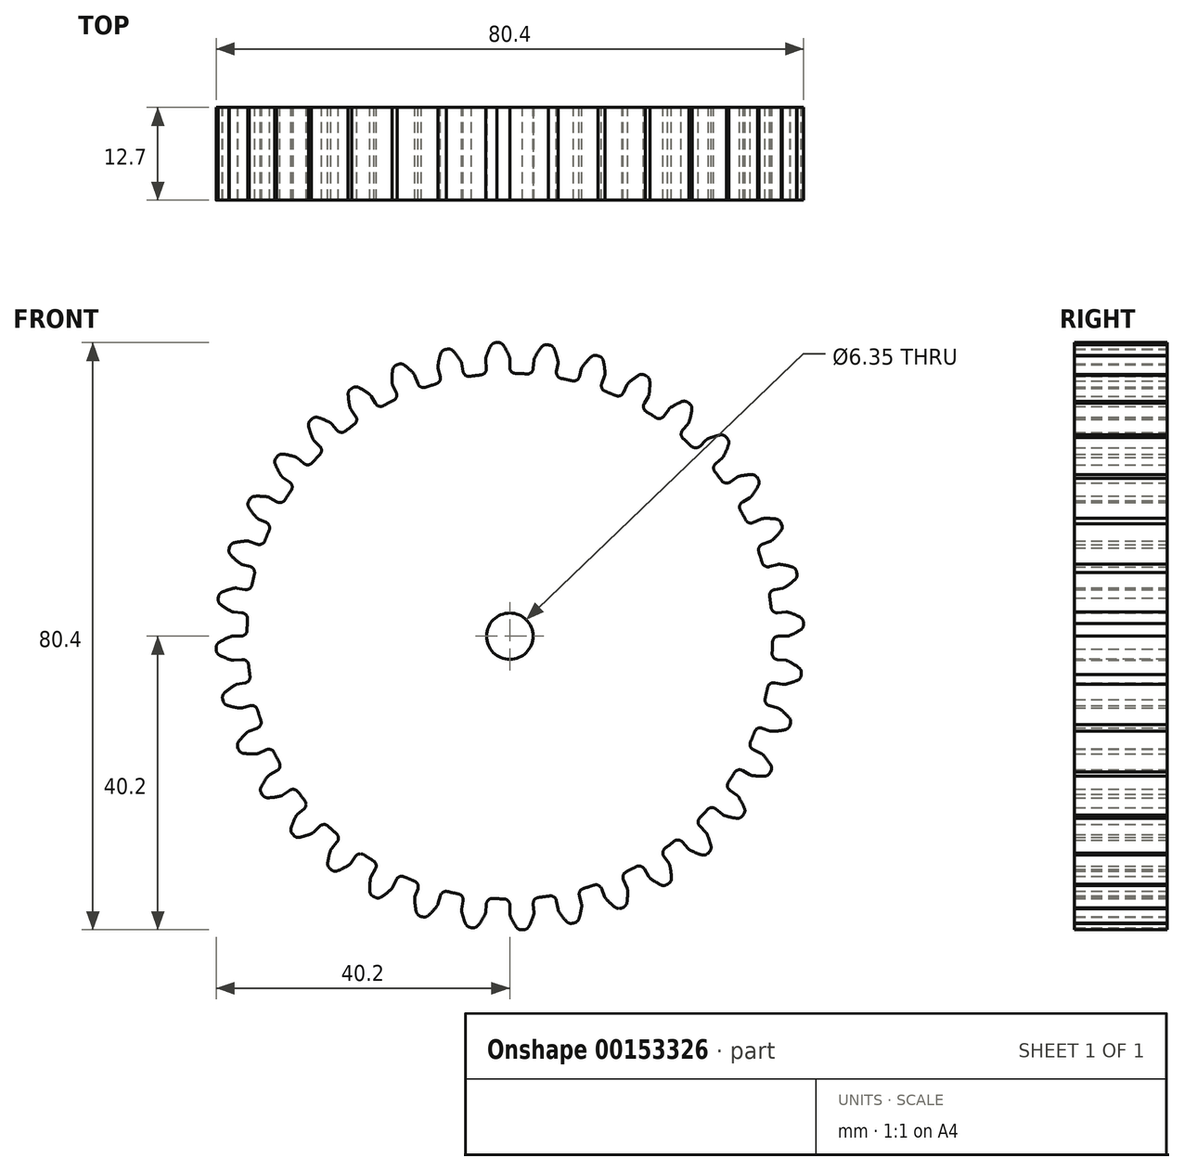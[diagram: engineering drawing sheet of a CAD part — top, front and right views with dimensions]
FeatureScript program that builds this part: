
annotation { "Feature Type Name" : "Feature", "Feature Type Description" : "" }
export const myFeature = defineFeature(function(context is Context, id is Id, definition is map)
    precondition{}
    {
        {
            var Q0;
            Q0=qCreatedBy(makeId("Front.planeOp"),FACE);
            var sketch = newSketch(context, id + "F0", { "sketchPlane" : qUnion([Q0])});
            skArc(sketch, "E0", {"start": v(-3.94, 35.77) * mm, "mid": v(-4.7, 35.68) * mm, "end": v(-5.45, 35.57) * mm});
            skLineSegment(sketch, "E1", {"start": v(-1.57, 40.2) * mm, "end": v(-1.76, 40.2) * mm});
            skLineSegment(sketch, "E2", {"start": v(0, 37.94) * mm, "end": v(0, 36.8) * mm});
            skArc(sketch, "E3.trimOffspring", {"start": v(-0.06, 38.25) * mm, "mid": v(-0.43, 39.06) * mm, "end": v(-0.87, 39.82) * mm});
            skLineSegment(sketch, "E4.MirrorCS", {"start": v(-1.94, 40.18) * mm, "end": v(-1.76, 40.2) * mm});
            skArc(sketch, "E5.MirrorCS", {"start": v(-3.27, 38.11) * mm, "mid": v(-2.98, 38.94) * mm, "end": v(-2.6, 39.75) * mm});
            skLineSegment(sketch, "E6.MirrorCS", {"start": v(-3.3, 37.8) * mm, "end": v(-3.2, 36.66) * mm});
            skPoint(sketch, "E7.visualSharp", {"position": v(0, 35.98) * mm});
            skArc(sketch, "E7.filletArc", {"start": v(0, 36.8) * mm, "mid": v(0.24, 36.22) * mm, "end": v(0.8, 35.97) * mm});
            skPoint(sketch, "E8.visualSharp", {"position": v(-3.14, 35.85) * mm});
            skArc(sketch, "E8.filletArc", {"start": v(-3.94, 35.77) * mm, "mid": v(-3.4, 36.06) * mm, "end": v(-3.2, 36.66) * mm});
            skPoint(sketch, "E9.visualSharp", {"position": v(-3.32, 37.96) * mm});
            skArc(sketch, "E9.filletArc", {"start": v(-3.27, 38.11) * mm, "mid": v(-3.3, 37.96) * mm, "end": v(-3.3, 37.8) * mm});
            skPoint(sketch, "E10.visualSharp", {"position": v(0, 38.1) * mm});
            skArc(sketch, "E10.filletArc", {"start": v(0, 37.94) * mm, "mid": v(-0.02, 38.1) * mm, "end": v(-0.06, 38.25) * mm});
            skPoint(sketch, "E11.visualSharp", {"position": v(-2.38, 40.15) * mm});
            skArc(sketch, "E11.filletArc", {"start": v(-1.94, 40.18) * mm, "mid": v(-2.33, 40.05) * mm, "end": v(-2.6, 39.75) * mm});
            skPoint(sketch, "E12.visualSharp", {"position": v(-1.13, 40.2) * mm});
            skArc(sketch, "E12.filletArc", {"start": v(-0.87, 39.82) * mm, "mid": v(-1.17, 40.1) * mm, "end": v(-1.57, 40.2) * mm});
            skArc(sketch, "E13.1.0", {"start": v(-10.1, 34.54) * mm, "mid": v(-9.6, 34.93) * mm, "end": v(-9.52, 35.55) * mm});
            skLineSegment(sketch, "E13.1.1", {"start": v(-9.82, 36.65) * mm, "end": v(-9.52, 35.55) * mm});
            skArc(sketch, "E13.1.2", {"start": v(-9.84, 36.96) * mm, "mid": v(-9.85, 36.8) * mm, "end": v(-9.82, 36.65) * mm});
            skArc(sketch, "E13.1.3", {"start": v(-9.84, 36.96) * mm, "mid": v(-9.7, 37.84) * mm, "end": v(-9.47, 38.69) * mm});
            skArc(sketch, "E13.1.4", {"start": v(-8.9, 39.24) * mm, "mid": v(-9.25, 39.04) * mm, "end": v(-9.47, 38.69) * mm});
            skLineSegment(sketch, "E13.1.5", {"start": v(-8.9, 39.24) * mm, "end": v(-8.7, 39.29) * mm});
            skLineSegment(sketch, "E13.1.6", {"start": v(-8.52, 39.32) * mm, "end": v(-8.7, 39.29) * mm});
            skArc(sketch, "E13.1.7", {"start": v(-7.77, 39.06) * mm, "mid": v(-8.12, 39.29) * mm, "end": v(-8.52, 39.32) * mm});
            skArc(sketch, "E13.1.8", {"start": v(-6.7, 37.66) * mm, "mid": v(-7.2, 38.39) * mm, "end": v(-7.77, 39.06) * mm});
            skArc(sketch, "E13.1.9", {"start": v(-6.59, 37.37) * mm, "mid": v(-6.63, 37.52) * mm, "end": v(-6.7, 37.66) * mm});
            skLineSegment(sketch, "E13.1.10", {"start": v(-6.59, 37.37) * mm, "end": v(-6.4, 36.24) * mm});
            skArc(sketch, "E13.1.11", {"start": v(-6.4, 36.24) * mm, "mid": v(-6.06, 35.71) * mm, "end": v(-5.45, 35.57) * mm});
            skArc(sketch, "E13.2.0", {"start": v(-15.93, 32.26) * mm, "mid": v(-15.52, 32.73) * mm, "end": v(-15.55, 33.35) * mm});
            skLineSegment(sketch, "E13.2.1", {"start": v(-16.04, 34.39) * mm, "end": v(-15.55, 33.35) * mm});
            skArc(sketch, "E13.2.2", {"start": v(-16.11, 34.7) * mm, "mid": v(-16.09, 34.54) * mm, "end": v(-16.04, 34.39) * mm});
            skArc(sketch, "E13.2.3", {"start": v(-16.11, 34.7) * mm, "mid": v(-16.12, 35.58) * mm, "end": v(-16.04, 36.46) * mm});
            skArc(sketch, "E13.2.4", {"start": v(-15.57, 37.1) * mm, "mid": v(-15.89, 36.84) * mm, "end": v(-16.04, 36.46) * mm});
            skLineSegment(sketch, "E13.2.5", {"start": v(-15.57, 37.1) * mm, "end": v(-15.4, 37.18) * mm});
            skLineSegment(sketch, "E13.2.6", {"start": v(-15.22, 37.24) * mm, "end": v(-15.4, 37.18) * mm});
            skArc(sketch, "E13.2.7", {"start": v(-14.44, 37.12) * mm, "mid": v(-14.81, 37.28) * mm, "end": v(-15.22, 37.24) * mm});
            skArc(sketch, "E13.2.8", {"start": v(-13.14, 35.93) * mm, "mid": v(-13.76, 36.55) * mm, "end": v(-14.44, 37.12) * mm});
            skArc(sketch, "E13.2.9", {"start": v(-12.98, 35.65) * mm, "mid": v(-13.05, 35.8) * mm, "end": v(-13.14, 35.93) * mm});
            skLineSegment(sketch, "E13.2.10", {"start": v(-12.98, 35.65) * mm, "end": v(-12.59, 34.58) * mm});
            skArc(sketch, "E13.2.11", {"start": v(-12.59, 34.58) * mm, "mid": v(-12.17, 34.12) * mm, "end": v(-11.55, 34.08) * mm});
            skArc(sketch, "E13.3.0", {"start": v(-21.3, 29) * mm, "mid": v(-20.97, 29.54) * mm, "end": v(-21.1, 30.14) * mm});
            skLineSegment(sketch, "E13.3.1", {"start": v(-21.76, 31.08) * mm, "end": v(-21.1, 30.14) * mm});
            skArc(sketch, "E13.3.2", {"start": v(-21.9, 31.37) * mm, "mid": v(-21.84, 31.22) * mm, "end": v(-21.76, 31.08) * mm});
            skArc(sketch, "E13.3.3", {"start": v(-21.9, 31.37) * mm, "mid": v(-22.05, 32.24) * mm, "end": v(-22.13, 33.12) * mm});
            skArc(sketch, "E13.3.4", {"start": v(-21.78, 33.83) * mm, "mid": v(-22.04, 33.52) * mm, "end": v(-22.13, 33.12) * mm});
            skLineSegment(sketch, "E13.3.5", {"start": v(-21.78, 33.83) * mm, "end": v(-21.62, 33.94) * mm});
            skLineSegment(sketch, "E13.3.6", {"start": v(-21.46, 34.03) * mm, "end": v(-21.62, 33.94) * mm});
            skArc(sketch, "E13.3.7", {"start": v(-20.66, 34.05) * mm, "mid": v(-21.06, 34.14) * mm, "end": v(-21.46, 34.03) * mm});
            skArc(sketch, "E13.3.8", {"start": v(-19.18, 33.1) * mm, "mid": v(-19.9, 33.6) * mm, "end": v(-20.66, 34.05) * mm});
            skArc(sketch, "E13.3.9", {"start": v(-18.97, 32.86) * mm, "mid": v(-19.06, 32.99) * mm, "end": v(-19.18, 33.1) * mm});
            skLineSegment(sketch, "E13.3.10", {"start": v(-18.97, 32.86) * mm, "end": v(-18.4, 31.87) * mm});
            skArc(sketch, "E13.3.11", {"start": v(-18.4, 31.87) * mm, "mid": v(-17.9, 31.49) * mm, "end": v(-17.29, 31.56) * mm});
            skArc(sketch, "E13.4.0", {"start": v(-26, 24.87) * mm, "mid": v(-25.78, 25.45) * mm, "end": v(-26.02, 26.02) * mm});
            skLineSegment(sketch, "E13.4.1", {"start": v(-26.83, 26.83) * mm, "end": v(-26.02, 26.02) * mm});
            skArc(sketch, "E13.4.2", {"start": v(-27, 27.1) * mm, "mid": v(-26.93, 26.95) * mm, "end": v(-26.83, 26.83) * mm});
            skArc(sketch, "E13.4.3", {"start": v(-27, 27.1) * mm, "mid": v(-27.31, 27.92) * mm, "end": v(-27.54, 28.77) * mm});
            skArc(sketch, "E13.4.4", {"start": v(-27.32, 29.53) * mm, "mid": v(-27.53, 29.18) * mm, "end": v(-27.54, 28.77) * mm});
            skLineSegment(sketch, "E13.4.5", {"start": v(-27.32, 29.53) * mm, "end": v(-27.19, 29.67) * mm});
            skLineSegment(sketch, "E13.4.6", {"start": v(-27.04, 29.79) * mm, "end": v(-27.19, 29.67) * mm});
            skArc(sketch, "E13.4.7", {"start": v(-26.26, 29.94) * mm, "mid": v(-26.67, 29.97) * mm, "end": v(-27.04, 29.79) * mm});
            skArc(sketch, "E13.4.8", {"start": v(-24.63, 29.26) * mm, "mid": v(-25.43, 29.64) * mm, "end": v(-26.26, 29.94) * mm});
            skArc(sketch, "E13.4.9", {"start": v(-24.39, 29.07) * mm, "mid": v(-24.5, 29.18) * mm, "end": v(-24.63, 29.26) * mm});
            skLineSegment(sketch, "E13.4.10", {"start": v(-24.39, 29.07) * mm, "end": v(-23.65, 28.2) * mm});
            skArc(sketch, "E13.4.11", {"start": v(-23.65, 28.2) * mm, "mid": v(-23.1, 27.9) * mm, "end": v(-22.5, 28.08) * mm});
            skArc(sketch, "E13.5.0", {"start": v(-29.93, 19.97) * mm, "mid": v(-29.8, 20.58) * mm, "end": v(-30.14, 21.1) * mm});
            skLineSegment(sketch, "E13.5.1", {"start": v(-31.08, 21.76) * mm, "end": v(-30.14, 21.1) * mm});
            skArc(sketch, "E13.5.2", {"start": v(-31.3, 22) * mm, "mid": v(-31.2, 21.87) * mm, "end": v(-31.08, 21.76) * mm});
            skArc(sketch, "E13.5.3", {"start": v(-31.3, 22) * mm, "mid": v(-31.75, 22.75) * mm, "end": v(-32.12, 23.55) * mm});
            skArc(sketch, "E13.5.4", {"start": v(-32.03, 24.34) * mm, "mid": v(-32.18, 23.96) * mm, "end": v(-32.12, 23.55) * mm});
            skLineSegment(sketch, "E13.5.5", {"start": v(-32.03, 24.34) * mm, "end": v(-31.92, 24.5) * mm});
            skLineSegment(sketch, "E13.5.6", {"start": v(-31.8, 24.64) * mm, "end": v(-31.92, 24.5) * mm});
            skArc(sketch, "E13.5.7", {"start": v(-31.06, 24.93) * mm, "mid": v(-31.47, 24.88) * mm, "end": v(-31.8, 24.64) * mm});
            skArc(sketch, "E13.5.8", {"start": v(-29.34, 24.54) * mm, "mid": v(-30.2, 24.78) * mm, "end": v(-31.06, 24.93) * mm});
            skArc(sketch, "E13.5.9", {"start": v(-29.07, 24.39) * mm, "mid": v(-29.2, 24.48) * mm, "end": v(-29.34, 24.54) * mm});
            skLineSegment(sketch, "E13.5.10", {"start": v(-29.07, 24.39) * mm, "end": v(-28.2, 23.65) * mm});
            skArc(sketch, "E13.5.11", {"start": v(-28.2, 23.65) * mm, "mid": v(-27.6, 23.46) * mm, "end": v(-27.04, 23.74) * mm});
            skArc(sketch, "E13.6.0", {"start": v(-32.94, 14.47) * mm, "mid": v(-32.93, 15.1) * mm, "end": v(-33.35, 15.55) * mm});
            skLineSegment(sketch, "E13.6.1", {"start": v(-34.39, 16.04) * mm, "end": v(-33.35, 15.55) * mm});
            skArc(sketch, "E13.6.2", {"start": v(-34.64, 16.22) * mm, "mid": v(-34.52, 16.12) * mm, "end": v(-34.39, 16.04) * mm});
            skArc(sketch, "E13.6.3", {"start": v(-34.64, 16.22) * mm, "mid": v(-35.21, 16.9) * mm, "end": v(-35.72, 17.62) * mm});
            skArc(sketch, "E13.6.4", {"start": v(-35.77, 18.4) * mm, "mid": v(-35.85, 18) * mm, "end": v(-35.72, 17.62) * mm});
            skLineSegment(sketch, "E13.6.5", {"start": v(-35.77, 18.4) * mm, "end": v(-35.7, 18.58) * mm});
            skLineSegment(sketch, "E13.6.6", {"start": v(-35.6, 18.74) * mm, "end": v(-35.7, 18.58) * mm});
            skArc(sketch, "E13.6.7", {"start": v(-34.92, 19.16) * mm, "mid": v(-35.31, 19.04) * mm, "end": v(-35.6, 18.74) * mm});
            skArc(sketch, "E13.6.8", {"start": v(-33.16, 19.07) * mm, "mid": v(-34.04, 19.16) * mm, "end": v(-34.92, 19.16) * mm});
            skArc(sketch, "E13.6.9", {"start": v(-32.86, 18.97) * mm, "mid": v(-33, 19.04) * mm, "end": v(-33.16, 19.07) * mm});
            skLineSegment(sketch, "E13.6.10", {"start": v(-32.86, 18.97) * mm, "end": v(-31.87, 18.4) * mm});
            skArc(sketch, "E13.6.11", {"start": v(-31.87, 18.4) * mm, "mid": v(-31.25, 18.31) * mm, "end": v(-30.75, 18.69) * mm});
            skArc(sketch, "E13.7.0", {"start": v(-34.96, 8.53) * mm, "mid": v(-35.05, 9.15) * mm, "end": v(-35.55, 9.52) * mm});
            skLineSegment(sketch, "E13.7.1", {"start": v(-36.65, 9.82) * mm, "end": v(-35.55, 9.52) * mm});
            skArc(sketch, "E13.7.2", {"start": v(-36.93, 9.96) * mm, "mid": v(-36.8, 9.88) * mm, "end": v(-36.65, 9.82) * mm});
            skArc(sketch, "E13.7.3", {"start": v(-36.93, 9.96) * mm, "mid": v(-37.61, 10.52) * mm, "end": v(-38.24, 11.15) * mm});
            skArc(sketch, "E13.7.4", {"start": v(-38.43, 11.92) * mm, "mid": v(-38.43, 11.5) * mm, "end": v(-38.24, 11.15) * mm});
            skLineSegment(sketch, "E13.7.5", {"start": v(-38.43, 11.92) * mm, "end": v(-38.38, 12.1) * mm});
            skLineSegment(sketch, "E13.7.6", {"start": v(-38.31, 12.28) * mm, "end": v(-38.38, 12.1) * mm});
            skArc(sketch, "E13.7.7", {"start": v(-37.72, 12.8) * mm, "mid": v(-38.08, 12.62) * mm, "end": v(-38.31, 12.28) * mm});
            skArc(sketch, "E13.7.8", {"start": v(-35.97, 13.03) * mm, "mid": v(-36.85, 12.95) * mm, "end": v(-37.72, 12.8) * mm});
            skArc(sketch, "E13.7.9", {"start": v(-35.65, 12.98) * mm, "mid": v(-35.8, 13.02) * mm, "end": v(-35.97, 13.03) * mm});
            skLineSegment(sketch, "E13.7.10", {"start": v(-35.65, 12.98) * mm, "end": v(-34.58, 12.59) * mm});
            skArc(sketch, "E13.7.11", {"start": v(-34.58, 12.59) * mm, "mid": v(-33.96, 12.6) * mm, "end": v(-33.53, 13.06) * mm});
            skArc(sketch, "E13.8.0", {"start": v(-35.9, 2.33) * mm, "mid": v(-36.1, 2.92) * mm, "end": v(-36.66, 3.2) * mm});
            skLineSegment(sketch, "E13.8.1", {"start": v(-37.8, 3.3) * mm, "end": v(-36.66, 3.2) * mm});
            skArc(sketch, "E13.8.2", {"start": v(-38.1, 3.4) * mm, "mid": v(-37.95, 3.34) * mm, "end": v(-37.8, 3.3) * mm});
            skArc(sketch, "E13.8.3", {"start": v(-38.1, 3.4) * mm, "mid": v(-38.87, 3.83) * mm, "end": v(-39.6, 4.34) * mm});
            skArc(sketch, "E13.8.4", {"start": v(-39.91, 5.06) * mm, "mid": v(-39.85, 4.66) * mm, "end": v(-39.6, 4.34) * mm});
            skLineSegment(sketch, "E13.8.5", {"start": v(-39.91, 5.06) * mm, "end": v(-39.9, 5.25) * mm});
            skLineSegment(sketch, "E13.8.6", {"start": v(-39.86, 5.44) * mm, "end": v(-39.9, 5.25) * mm});
            skArc(sketch, "E13.8.7", {"start": v(-39.37, 6.06) * mm, "mid": v(-39.7, 5.81) * mm, "end": v(-39.86, 5.44) * mm});
            skArc(sketch, "E13.8.8", {"start": v(-37.68, 6.58) * mm, "mid": v(-38.54, 6.36) * mm, "end": v(-39.37, 6.06) * mm});
            skArc(sketch, "E13.8.9", {"start": v(-37.37, 6.59) * mm, "mid": v(-37.52, 6.6) * mm, "end": v(-37.68, 6.58) * mm});
            skLineSegment(sketch, "E13.8.10", {"start": v(-37.37, 6.59) * mm, "end": v(-36.24, 6.4) * mm});
            skArc(sketch, "E13.8.11", {"start": v(-36.24, 6.4) * mm, "mid": v(-35.63, 6.52) * mm, "end": v(-35.29, 7.04) * mm});
            skArc(sketch, "E13.9.0", {"start": v(-35.77, -3.94) * mm, "mid": v(-36.06, -3.4) * mm, "end": v(-36.66, -3.2) * mm});
            skLineSegment(sketch, "E13.9.1", {"start": v(-37.8, -3.3) * mm, "end": v(-36.66, -3.2) * mm});
            skArc(sketch, "E13.9.2", {"start": v(-38.11, -3.27) * mm, "mid": v(-37.96, -3.3) * mm, "end": v(-37.8, -3.3) * mm});
            skArc(sketch, "E13.9.3", {"start": v(-38.11, -3.27) * mm, "mid": v(-38.94, -2.98) * mm, "end": v(-39.75, -2.6) * mm});
            skArc(sketch, "E13.9.4", {"start": v(-40.18, -1.94) * mm, "mid": v(-40.05, -2.33) * mm, "end": v(-39.75, -2.6) * mm});
            skLineSegment(sketch, "E13.9.5", {"start": v(-40.18, -1.94) * mm, "end": v(-40.2, -1.76) * mm});
            skLineSegment(sketch, "E13.9.6", {"start": v(-40.2, -1.57) * mm, "end": v(-40.2, -1.76) * mm});
            skArc(sketch, "E13.9.7", {"start": v(-39.82, -0.87) * mm, "mid": v(-40.1, -1.17) * mm, "end": v(-40.2, -1.57) * mm});
            skArc(sketch, "E13.9.8", {"start": v(-38.25, -0.06) * mm, "mid": v(-39.06, -0.43) * mm, "end": v(-39.82, -0.87) * mm});
            skArc(sketch, "E13.9.9", {"start": v(-37.94, 0) * mm, "mid": v(-38.1, -0.02) * mm, "end": v(-38.25, -0.06) * mm});
            skLineSegment(sketch, "E13.9.10", {"start": v(-37.94, 0) * mm, "end": v(-36.8, 0) * mm});
            skArc(sketch, "E13.9.11", {"start": v(-36.8, 0) * mm, "mid": v(-36.22, 0.24) * mm, "end": v(-35.97, 0.8) * mm});
            skArc(sketch, "E13.10.0", {"start": v(-34.54, -10.1) * mm, "mid": v(-34.93, -9.6) * mm, "end": v(-35.55, -9.52) * mm});
            skLineSegment(sketch, "E13.10.1", {"start": v(-36.65, -9.82) * mm, "end": v(-35.55, -9.52) * mm});
            skArc(sketch, "E13.10.2", {"start": v(-36.96, -9.84) * mm, "mid": v(-36.8, -9.85) * mm, "end": v(-36.65, -9.82) * mm});
            skArc(sketch, "E13.10.3", {"start": v(-36.96, -9.84) * mm, "mid": v(-37.84, -9.7) * mm, "end": v(-38.69, -9.47) * mm});
            skArc(sketch, "E13.10.4", {"start": v(-39.24, -8.9) * mm, "mid": v(-39.04, -9.25) * mm, "end": v(-38.69, -9.47) * mm});
            skLineSegment(sketch, "E13.10.5", {"start": v(-39.24, -8.9) * mm, "end": v(-39.29, -8.7) * mm});
            skLineSegment(sketch, "E13.10.6", {"start": v(-39.32, -8.52) * mm, "end": v(-39.29, -8.7) * mm});
            skArc(sketch, "E13.10.7", {"start": v(-39.06, -7.77) * mm, "mid": v(-39.29, -8.12) * mm, "end": v(-39.32, -8.52) * mm});
            skArc(sketch, "E13.10.8", {"start": v(-37.66, -6.7) * mm, "mid": v(-38.39, -7.2) * mm, "end": v(-39.06, -7.77) * mm});
            skArc(sketch, "E13.10.9", {"start": v(-37.37, -6.59) * mm, "mid": v(-37.52, -6.63) * mm, "end": v(-37.66, -6.7) * mm});
            skLineSegment(sketch, "E13.10.10", {"start": v(-37.37, -6.59) * mm, "end": v(-36.24, -6.4) * mm});
            skArc(sketch, "E13.10.11", {"start": v(-36.24, -6.4) * mm, "mid": v(-35.71, -6.06) * mm, "end": v(-35.57, -5.45) * mm});
            skArc(sketch, "E13.11.0", {"start": v(-32.26, -15.93) * mm, "mid": v(-32.73, -15.52) * mm, "end": v(-33.35, -15.55) * mm});
            skLineSegment(sketch, "E13.11.1", {"start": v(-34.39, -16.04) * mm, "end": v(-33.35, -15.55) * mm});
            skArc(sketch, "E13.11.2", {"start": v(-34.7, -16.11) * mm, "mid": v(-34.54, -16.09) * mm, "end": v(-34.39, -16.04) * mm});
            skArc(sketch, "E13.11.3", {"start": v(-34.7, -16.11) * mm, "mid": v(-35.58, -16.12) * mm, "end": v(-36.46, -16.04) * mm});
            skArc(sketch, "E13.11.4", {"start": v(-37.1, -15.57) * mm, "mid": v(-36.84, -15.89) * mm, "end": v(-36.46, -16.04) * mm});
            skLineSegment(sketch, "E13.11.5", {"start": v(-37.1, -15.57) * mm, "end": v(-37.18, -15.4) * mm});
            skLineSegment(sketch, "E13.11.6", {"start": v(-37.24, -15.22) * mm, "end": v(-37.18, -15.4) * mm});
            skArc(sketch, "E13.11.7", {"start": v(-37.12, -14.44) * mm, "mid": v(-37.28, -14.81) * mm, "end": v(-37.24, -15.22) * mm});
            skArc(sketch, "E13.11.8", {"start": v(-35.93, -13.14) * mm, "mid": v(-36.55, -13.76) * mm, "end": v(-37.12, -14.44) * mm});
            skArc(sketch, "E13.11.9", {"start": v(-35.65, -12.98) * mm, "mid": v(-35.8, -13.05) * mm, "end": v(-35.93, -13.14) * mm});
            skLineSegment(sketch, "E13.11.10", {"start": v(-35.65, -12.98) * mm, "end": v(-34.58, -12.59) * mm});
            skArc(sketch, "E13.11.11", {"start": v(-34.58, -12.59) * mm, "mid": v(-34.12, -12.17) * mm, "end": v(-34.08, -11.55) * mm});
            skArc(sketch, "E13.12.0", {"start": v(-29, -21.3) * mm, "mid": v(-29.54, -20.97) * mm, "end": v(-30.14, -21.1) * mm});
            skLineSegment(sketch, "E13.12.1", {"start": v(-31.08, -21.76) * mm, "end": v(-30.14, -21.1) * mm});
            skArc(sketch, "E13.12.2", {"start": v(-31.37, -21.9) * mm, "mid": v(-31.22, -21.84) * mm, "end": v(-31.08, -21.76) * mm});
            skArc(sketch, "E13.12.3", {"start": v(-31.37, -21.9) * mm, "mid": v(-32.24, -22.05) * mm, "end": v(-33.12, -22.13) * mm});
            skArc(sketch, "E13.12.4", {"start": v(-33.83, -21.78) * mm, "mid": v(-33.52, -22.04) * mm, "end": v(-33.12, -22.13) * mm});
            skLineSegment(sketch, "E13.12.5", {"start": v(-33.83, -21.78) * mm, "end": v(-33.94, -21.62) * mm});
            skLineSegment(sketch, "E13.12.6", {"start": v(-34.03, -21.46) * mm, "end": v(-33.94, -21.62) * mm});
            skArc(sketch, "E13.12.7", {"start": v(-34.05, -20.66) * mm, "mid": v(-34.14, -21.06) * mm, "end": v(-34.03, -21.46) * mm});
            skArc(sketch, "E13.12.8", {"start": v(-33.1, -19.18) * mm, "mid": v(-33.6, -19.9) * mm, "end": v(-34.05, -20.66) * mm});
            skArc(sketch, "E13.12.9", {"start": v(-32.86, -18.97) * mm, "mid": v(-32.99, -19.06) * mm, "end": v(-33.1, -19.18) * mm});
            skLineSegment(sketch, "E13.12.10", {"start": v(-32.86, -18.97) * mm, "end": v(-31.87, -18.4) * mm});
            skArc(sketch, "E13.12.11", {"start": v(-31.87, -18.4) * mm, "mid": v(-31.49, -17.9) * mm, "end": v(-31.56, -17.29) * mm});
            skArc(sketch, "E13.13.0", {"start": v(-24.87, -26) * mm, "mid": v(-25.45, -25.78) * mm, "end": v(-26.02, -26.02) * mm});
            skLineSegment(sketch, "E13.13.1", {"start": v(-26.83, -26.83) * mm, "end": v(-26.02, -26.02) * mm});
            skArc(sketch, "E13.13.2", {"start": v(-27.1, -27) * mm, "mid": v(-26.95, -26.93) * mm, "end": v(-26.83, -26.83) * mm});
            skArc(sketch, "E13.13.3", {"start": v(-27.1, -27) * mm, "mid": v(-27.92, -27.31) * mm, "end": v(-28.77, -27.54) * mm});
            skArc(sketch, "E13.13.4", {"start": v(-29.53, -27.32) * mm, "mid": v(-29.18, -27.53) * mm, "end": v(-28.77, -27.54) * mm});
            skLineSegment(sketch, "E13.13.5", {"start": v(-29.53, -27.32) * mm, "end": v(-29.67, -27.19) * mm});
            skLineSegment(sketch, "E13.13.6", {"start": v(-29.79, -27.04) * mm, "end": v(-29.67, -27.19) * mm});
            skArc(sketch, "E13.13.7", {"start": v(-29.94, -26.26) * mm, "mid": v(-29.97, -26.67) * mm, "end": v(-29.79, -27.04) * mm});
            skArc(sketch, "E13.13.8", {"start": v(-29.26, -24.63) * mm, "mid": v(-29.64, -25.43) * mm, "end": v(-29.94, -26.26) * mm});
            skArc(sketch, "E13.13.9", {"start": v(-29.07, -24.39) * mm, "mid": v(-29.18, -24.5) * mm, "end": v(-29.26, -24.63) * mm});
            skLineSegment(sketch, "E13.13.10", {"start": v(-29.07, -24.39) * mm, "end": v(-28.2, -23.65) * mm});
            skArc(sketch, "E13.13.11", {"start": v(-28.2, -23.65) * mm, "mid": v(-27.9, -23.1) * mm, "end": v(-28.08, -22.5) * mm});
            skArc(sketch, "E13.14.0", {"start": v(-19.97, -29.93) * mm, "mid": v(-20.58, -29.8) * mm, "end": v(-21.1, -30.14) * mm});
            skLineSegment(sketch, "E13.14.1", {"start": v(-21.76, -31.08) * mm, "end": v(-21.1, -30.14) * mm});
            skArc(sketch, "E13.14.2", {"start": v(-22, -31.3) * mm, "mid": v(-21.87, -31.2) * mm, "end": v(-21.76, -31.08) * mm});
            skArc(sketch, "E13.14.3", {"start": v(-22, -31.3) * mm, "mid": v(-22.75, -31.75) * mm, "end": v(-23.55, -32.12) * mm});
            skArc(sketch, "E13.14.4", {"start": v(-24.34, -32.03) * mm, "mid": v(-23.96, -32.18) * mm, "end": v(-23.55, -32.12) * mm});
            skLineSegment(sketch, "E13.14.5", {"start": v(-24.34, -32.03) * mm, "end": v(-24.5, -31.92) * mm});
            skLineSegment(sketch, "E13.14.6", {"start": v(-24.64, -31.8) * mm, "end": v(-24.5, -31.92) * mm});
            skArc(sketch, "E13.14.7", {"start": v(-24.93, -31.06) * mm, "mid": v(-24.88, -31.47) * mm, "end": v(-24.64, -31.8) * mm});
            skArc(sketch, "E13.14.8", {"start": v(-24.54, -29.34) * mm, "mid": v(-24.78, -30.2) * mm, "end": v(-24.93, -31.06) * mm});
            skArc(sketch, "E13.14.9", {"start": v(-24.39, -29.07) * mm, "mid": v(-24.48, -29.2) * mm, "end": v(-24.54, -29.34) * mm});
            skLineSegment(sketch, "E13.14.10", {"start": v(-24.39, -29.07) * mm, "end": v(-23.65, -28.2) * mm});
            skArc(sketch, "E13.14.11", {"start": v(-23.65, -28.2) * mm, "mid": v(-23.46, -27.6) * mm, "end": v(-23.74, -27.04) * mm});
            skArc(sketch, "E13.15.0", {"start": v(-14.47, -32.94) * mm, "mid": v(-15.1, -32.93) * mm, "end": v(-15.55, -33.35) * mm});
            skLineSegment(sketch, "E13.15.1", {"start": v(-16.04, -34.39) * mm, "end": v(-15.55, -33.35) * mm});
            skArc(sketch, "E13.15.2", {"start": v(-16.22, -34.64) * mm, "mid": v(-16.12, -34.52) * mm, "end": v(-16.04, -34.39) * mm});
            skArc(sketch, "E13.15.3", {"start": v(-16.22, -34.64) * mm, "mid": v(-16.9, -35.21) * mm, "end": v(-17.62, -35.72) * mm});
            skArc(sketch, "E13.15.4", {"start": v(-18.4, -35.77) * mm, "mid": v(-18, -35.85) * mm, "end": v(-17.62, -35.72) * mm});
            skLineSegment(sketch, "E13.15.5", {"start": v(-18.4, -35.77) * mm, "end": v(-18.58, -35.7) * mm});
            skLineSegment(sketch, "E13.15.6", {"start": v(-18.74, -35.6) * mm, "end": v(-18.58, -35.7) * mm});
            skArc(sketch, "E13.15.7", {"start": v(-19.16, -34.92) * mm, "mid": v(-19.04, -35.31) * mm, "end": v(-18.74, -35.6) * mm});
            skArc(sketch, "E13.15.8", {"start": v(-19.07, -33.16) * mm, "mid": v(-19.16, -34.04) * mm, "end": v(-19.16, -34.92) * mm});
            skArc(sketch, "E13.15.9", {"start": v(-18.97, -32.86) * mm, "mid": v(-19.04, -33) * mm, "end": v(-19.07, -33.16) * mm});
            skLineSegment(sketch, "E13.15.10", {"start": v(-18.97, -32.86) * mm, "end": v(-18.4, -31.87) * mm});
            skArc(sketch, "E13.15.11", {"start": v(-18.4, -31.87) * mm, "mid": v(-18.31, -31.25) * mm, "end": v(-18.69, -30.75) * mm});
            skArc(sketch, "E13.16.0", {"start": v(-8.53, -34.96) * mm, "mid": v(-9.15, -35.05) * mm, "end": v(-9.52, -35.55) * mm});
            skLineSegment(sketch, "E13.16.1", {"start": v(-9.82, -36.65) * mm, "end": v(-9.52, -35.55) * mm});
            skArc(sketch, "E13.16.2", {"start": v(-9.96, -36.93) * mm, "mid": v(-9.88, -36.8) * mm, "end": v(-9.82, -36.65) * mm});
            skArc(sketch, "E13.16.3", {"start": v(-9.96, -36.93) * mm, "mid": v(-10.52, -37.61) * mm, "end": v(-11.15, -38.24) * mm});
            skArc(sketch, "E13.16.4", {"start": v(-11.92, -38.43) * mm, "mid": v(-11.5, -38.43) * mm, "end": v(-11.15, -38.24) * mm});
            skLineSegment(sketch, "E13.16.5", {"start": v(-11.92, -38.43) * mm, "end": v(-12.1, -38.38) * mm});
            skLineSegment(sketch, "E13.16.6", {"start": v(-12.28, -38.31) * mm, "end": v(-12.1, -38.38) * mm});
            skArc(sketch, "E13.16.7", {"start": v(-12.8, -37.72) * mm, "mid": v(-12.62, -38.08) * mm, "end": v(-12.28, -38.31) * mm});
            skArc(sketch, "E13.16.8", {"start": v(-13.03, -35.97) * mm, "mid": v(-12.95, -36.85) * mm, "end": v(-12.8, -37.72) * mm});
            skArc(sketch, "E13.16.9", {"start": v(-12.98, -35.65) * mm, "mid": v(-13.02, -35.8) * mm, "end": v(-13.03, -35.97) * mm});
            skLineSegment(sketch, "E13.16.10", {"start": v(-12.98, -35.65) * mm, "end": v(-12.59, -34.58) * mm});
            skArc(sketch, "E13.16.11", {"start": v(-12.59, -34.58) * mm, "mid": v(-12.6, -33.96) * mm, "end": v(-13.06, -33.53) * mm});
            skArc(sketch, "E13.17.0", {"start": v(-2.33, -35.9) * mm, "mid": v(-2.92, -36.1) * mm, "end": v(-3.2, -36.66) * mm});
            skLineSegment(sketch, "E13.17.1", {"start": v(-3.3, -37.8) * mm, "end": v(-3.2, -36.66) * mm});
            skArc(sketch, "E13.17.2", {"start": v(-3.4, -38.1) * mm, "mid": v(-3.34, -37.95) * mm, "end": v(-3.3, -37.8) * mm});
            skArc(sketch, "E13.17.3", {"start": v(-3.4, -38.1) * mm, "mid": v(-3.83, -38.87) * mm, "end": v(-4.34, -39.6) * mm});
            skArc(sketch, "E13.17.4", {"start": v(-5.06, -39.91) * mm, "mid": v(-4.66, -39.85) * mm, "end": v(-4.34, -39.6) * mm});
            skLineSegment(sketch, "E13.17.5", {"start": v(-5.06, -39.91) * mm, "end": v(-5.25, -39.9) * mm});
            skLineSegment(sketch, "E13.17.6", {"start": v(-5.44, -39.86) * mm, "end": v(-5.25, -39.9) * mm});
            skArc(sketch, "E13.17.7", {"start": v(-6.06, -39.37) * mm, "mid": v(-5.81, -39.7) * mm, "end": v(-5.44, -39.86) * mm});
            skArc(sketch, "E13.17.8", {"start": v(-6.58, -37.68) * mm, "mid": v(-6.36, -38.54) * mm, "end": v(-6.06, -39.37) * mm});
            skArc(sketch, "E13.17.9", {"start": v(-6.59, -37.37) * mm, "mid": v(-6.6, -37.52) * mm, "end": v(-6.58, -37.68) * mm});
            skLineSegment(sketch, "E13.17.10", {"start": v(-6.59, -37.37) * mm, "end": v(-6.4, -36.24) * mm});
            skArc(sketch, "E13.17.11", {"start": v(-6.4, -36.24) * mm, "mid": v(-6.52, -35.63) * mm, "end": v(-7.04, -35.29) * mm});
            skArc(sketch, "E13.18.0", {"start": v(3.94, -35.77) * mm, "mid": v(3.4, -36.06) * mm, "end": v(3.2, -36.66) * mm});
            skLineSegment(sketch, "E13.18.1", {"start": v(3.3, -37.8) * mm, "end": v(3.2, -36.66) * mm});
            skArc(sketch, "E13.18.2", {"start": v(3.27, -38.11) * mm, "mid": v(3.3, -37.96) * mm, "end": v(3.3, -37.8) * mm});
            skArc(sketch, "E13.18.3", {"start": v(3.27, -38.11) * mm, "mid": v(2.98, -38.94) * mm, "end": v(2.6, -39.75) * mm});
            skArc(sketch, "E13.18.4", {"start": v(1.94, -40.18) * mm, "mid": v(2.33, -40.05) * mm, "end": v(2.6, -39.75) * mm});
            skLineSegment(sketch, "E13.18.5", {"start": v(1.94, -40.18) * mm, "end": v(1.76, -40.2) * mm});
            skLineSegment(sketch, "E13.18.6", {"start": v(1.57, -40.2) * mm, "end": v(1.76, -40.2) * mm});
            skArc(sketch, "E13.18.7", {"start": v(0.87, -39.82) * mm, "mid": v(1.17, -40.1) * mm, "end": v(1.57, -40.2) * mm});
            skArc(sketch, "E13.18.8", {"start": v(0.06, -38.25) * mm, "mid": v(0.43, -39.06) * mm, "end": v(0.87, -39.82) * mm});
            skArc(sketch, "E13.18.9", {"start": v(0, -37.94) * mm, "mid": v(0.02, -38.1) * mm, "end": v(0.06, -38.25) * mm});
            skLineSegment(sketch, "E13.18.10", {"start": v(0, -37.94) * mm, "end": v(0, -36.8) * mm});
            skArc(sketch, "E13.18.11", {"start": v(0, -36.8) * mm, "mid": v(-0.24, -36.22) * mm, "end": v(-0.8, -35.97) * mm});
            skArc(sketch, "E13.19.0", {"start": v(10.1, -34.54) * mm, "mid": v(9.6, -34.93) * mm, "end": v(9.52, -35.55) * mm});
            skLineSegment(sketch, "E13.19.1", {"start": v(9.82, -36.65) * mm, "end": v(9.52, -35.55) * mm});
            skArc(sketch, "E13.19.2", {"start": v(9.84, -36.96) * mm, "mid": v(9.85, -36.8) * mm, "end": v(9.82, -36.65) * mm});
            skArc(sketch, "E13.19.3", {"start": v(9.84, -36.96) * mm, "mid": v(9.7, -37.84) * mm, "end": v(9.47, -38.69) * mm});
            skArc(sketch, "E13.19.4", {"start": v(8.9, -39.24) * mm, "mid": v(9.25, -39.04) * mm, "end": v(9.47, -38.69) * mm});
            skLineSegment(sketch, "E13.19.5", {"start": v(8.9, -39.24) * mm, "end": v(8.7, -39.29) * mm});
            skLineSegment(sketch, "E13.19.6", {"start": v(8.52, -39.32) * mm, "end": v(8.7, -39.29) * mm});
            skArc(sketch, "E13.19.7", {"start": v(7.77, -39.06) * mm, "mid": v(8.12, -39.29) * mm, "end": v(8.52, -39.32) * mm});
            skArc(sketch, "E13.19.8", {"start": v(6.7, -37.66) * mm, "mid": v(7.2, -38.39) * mm, "end": v(7.77, -39.06) * mm});
            skArc(sketch, "E13.19.9", {"start": v(6.59, -37.37) * mm, "mid": v(6.63, -37.52) * mm, "end": v(6.7, -37.66) * mm});
            skLineSegment(sketch, "E13.19.10", {"start": v(6.59, -37.37) * mm, "end": v(6.4, -36.24) * mm});
            skArc(sketch, "E13.19.11", {"start": v(6.4, -36.24) * mm, "mid": v(6.06, -35.71) * mm, "end": v(5.45, -35.57) * mm});
            skArc(sketch, "E13.20.0", {"start": v(15.93, -32.26) * mm, "mid": v(15.52, -32.73) * mm, "end": v(15.55, -33.35) * mm});
            skLineSegment(sketch, "E13.20.1", {"start": v(16.04, -34.39) * mm, "end": v(15.55, -33.35) * mm});
            skArc(sketch, "E13.20.2", {"start": v(16.11, -34.7) * mm, "mid": v(16.09, -34.54) * mm, "end": v(16.04, -34.39) * mm});
            skArc(sketch, "E13.20.3", {"start": v(16.11, -34.7) * mm, "mid": v(16.12, -35.58) * mm, "end": v(16.04, -36.46) * mm});
            skArc(sketch, "E13.20.4", {"start": v(15.57, -37.1) * mm, "mid": v(15.89, -36.84) * mm, "end": v(16.04, -36.46) * mm});
            skLineSegment(sketch, "E13.20.5", {"start": v(15.57, -37.1) * mm, "end": v(15.4, -37.18) * mm});
            skLineSegment(sketch, "E13.20.6", {"start": v(15.22, -37.24) * mm, "end": v(15.4, -37.18) * mm});
            skArc(sketch, "E13.20.7", {"start": v(14.44, -37.12) * mm, "mid": v(14.81, -37.28) * mm, "end": v(15.22, -37.24) * mm});
            skArc(sketch, "E13.20.8", {"start": v(13.14, -35.93) * mm, "mid": v(13.76, -36.55) * mm, "end": v(14.44, -37.12) * mm});
            skArc(sketch, "E13.20.9", {"start": v(12.98, -35.65) * mm, "mid": v(13.05, -35.8) * mm, "end": v(13.14, -35.93) * mm});
            skLineSegment(sketch, "E13.20.10", {"start": v(12.98, -35.65) * mm, "end": v(12.59, -34.58) * mm});
            skArc(sketch, "E13.20.11", {"start": v(12.59, -34.58) * mm, "mid": v(12.17, -34.12) * mm, "end": v(11.55, -34.08) * mm});
            skArc(sketch, "E13.21.0", {"start": v(21.3, -29) * mm, "mid": v(20.97, -29.54) * mm, "end": v(21.1, -30.14) * mm});
            skLineSegment(sketch, "E13.21.1", {"start": v(21.76, -31.08) * mm, "end": v(21.1, -30.14) * mm});
            skArc(sketch, "E13.21.2", {"start": v(21.9, -31.37) * mm, "mid": v(21.84, -31.22) * mm, "end": v(21.76, -31.08) * mm});
            skArc(sketch, "E13.21.3", {"start": v(21.9, -31.37) * mm, "mid": v(22.05, -32.24) * mm, "end": v(22.13, -33.12) * mm});
            skArc(sketch, "E13.21.4", {"start": v(21.78, -33.83) * mm, "mid": v(22.04, -33.52) * mm, "end": v(22.13, -33.12) * mm});
            skLineSegment(sketch, "E13.21.5", {"start": v(21.78, -33.83) * mm, "end": v(21.62, -33.94) * mm});
            skLineSegment(sketch, "E13.21.6", {"start": v(21.46, -34.03) * mm, "end": v(21.62, -33.94) * mm});
            skArc(sketch, "E13.21.7", {"start": v(20.66, -34.05) * mm, "mid": v(21.06, -34.14) * mm, "end": v(21.46, -34.03) * mm});
            skArc(sketch, "E13.21.8", {"start": v(19.18, -33.1) * mm, "mid": v(19.9, -33.6) * mm, "end": v(20.66, -34.05) * mm});
            skArc(sketch, "E13.21.9", {"start": v(18.97, -32.86) * mm, "mid": v(19.06, -32.99) * mm, "end": v(19.18, -33.1) * mm});
            skLineSegment(sketch, "E13.21.10", {"start": v(18.97, -32.86) * mm, "end": v(18.4, -31.87) * mm});
            skArc(sketch, "E13.21.11", {"start": v(18.4, -31.87) * mm, "mid": v(17.9, -31.49) * mm, "end": v(17.29, -31.56) * mm});
            skArc(sketch, "E13.22.0", {"start": v(26, -24.87) * mm, "mid": v(25.78, -25.45) * mm, "end": v(26.02, -26.02) * mm});
            skLineSegment(sketch, "E13.22.1", {"start": v(26.83, -26.83) * mm, "end": v(26.02, -26.02) * mm});
            skArc(sketch, "E13.22.2", {"start": v(27, -27.1) * mm, "mid": v(26.93, -26.95) * mm, "end": v(26.83, -26.83) * mm});
            skArc(sketch, "E13.22.3", {"start": v(27, -27.1) * mm, "mid": v(27.31, -27.92) * mm, "end": v(27.54, -28.77) * mm});
            skArc(sketch, "E13.22.4", {"start": v(27.32, -29.53) * mm, "mid": v(27.53, -29.18) * mm, "end": v(27.54, -28.77) * mm});
            skLineSegment(sketch, "E13.22.5", {"start": v(27.32, -29.53) * mm, "end": v(27.19, -29.67) * mm});
            skLineSegment(sketch, "E13.22.6", {"start": v(27.04, -29.79) * mm, "end": v(27.19, -29.67) * mm});
            skArc(sketch, "E13.22.7", {"start": v(26.26, -29.94) * mm, "mid": v(26.67, -29.97) * mm, "end": v(27.04, -29.79) * mm});
            skArc(sketch, "E13.22.8", {"start": v(24.63, -29.26) * mm, "mid": v(25.43, -29.64) * mm, "end": v(26.26, -29.94) * mm});
            skArc(sketch, "E13.22.9", {"start": v(24.39, -29.07) * mm, "mid": v(24.5, -29.18) * mm, "end": v(24.63, -29.26) * mm});
            skLineSegment(sketch, "E13.22.10", {"start": v(24.39, -29.07) * mm, "end": v(23.65, -28.2) * mm});
            skArc(sketch, "E13.22.11", {"start": v(23.65, -28.2) * mm, "mid": v(23.1, -27.9) * mm, "end": v(22.5, -28.08) * mm});
            skArc(sketch, "E13.23.0", {"start": v(29.93, -19.97) * mm, "mid": v(29.8, -20.58) * mm, "end": v(30.14, -21.1) * mm});
            skLineSegment(sketch, "E13.23.1", {"start": v(31.08, -21.76) * mm, "end": v(30.14, -21.1) * mm});
            skArc(sketch, "E13.23.2", {"start": v(31.3, -22) * mm, "mid": v(31.2, -21.87) * mm, "end": v(31.08, -21.76) * mm});
            skArc(sketch, "E13.23.3", {"start": v(31.3, -22) * mm, "mid": v(31.75, -22.75) * mm, "end": v(32.12, -23.55) * mm});
            skArc(sketch, "E13.23.4", {"start": v(32.03, -24.34) * mm, "mid": v(32.18, -23.96) * mm, "end": v(32.12, -23.55) * mm});
            skLineSegment(sketch, "E13.23.5", {"start": v(32.03, -24.34) * mm, "end": v(31.92, -24.5) * mm});
            skLineSegment(sketch, "E13.23.6", {"start": v(31.8, -24.64) * mm, "end": v(31.92, -24.5) * mm});
            skArc(sketch, "E13.23.7", {"start": v(31.06, -24.93) * mm, "mid": v(31.47, -24.88) * mm, "end": v(31.8, -24.64) * mm});
            skArc(sketch, "E13.23.8", {"start": v(29.34, -24.54) * mm, "mid": v(30.2, -24.78) * mm, "end": v(31.06, -24.93) * mm});
            skArc(sketch, "E13.23.9", {"start": v(29.07, -24.39) * mm, "mid": v(29.2, -24.48) * mm, "end": v(29.34, -24.54) * mm});
            skLineSegment(sketch, "E13.23.10", {"start": v(29.07, -24.39) * mm, "end": v(28.2, -23.65) * mm});
            skArc(sketch, "E13.23.11", {"start": v(28.2, -23.65) * mm, "mid": v(27.6, -23.46) * mm, "end": v(27.04, -23.74) * mm});
            skArc(sketch, "E13.24.0", {"start": v(32.94, -14.47) * mm, "mid": v(32.93, -15.1) * mm, "end": v(33.35, -15.55) * mm});
            skLineSegment(sketch, "E13.24.1", {"start": v(34.39, -16.04) * mm, "end": v(33.35, -15.55) * mm});
            skArc(sketch, "E13.24.2", {"start": v(34.64, -16.22) * mm, "mid": v(34.52, -16.12) * mm, "end": v(34.39, -16.04) * mm});
            skArc(sketch, "E13.24.3", {"start": v(34.64, -16.22) * mm, "mid": v(35.21, -16.9) * mm, "end": v(35.72, -17.62) * mm});
            skArc(sketch, "E13.24.4", {"start": v(35.77, -18.4) * mm, "mid": v(35.85, -18) * mm, "end": v(35.72, -17.62) * mm});
            skLineSegment(sketch, "E13.24.5", {"start": v(35.77, -18.4) * mm, "end": v(35.7, -18.58) * mm});
            skLineSegment(sketch, "E13.24.6", {"start": v(35.6, -18.74) * mm, "end": v(35.7, -18.58) * mm});
            skArc(sketch, "E13.24.7", {"start": v(34.92, -19.16) * mm, "mid": v(35.31, -19.04) * mm, "end": v(35.6, -18.74) * mm});
            skArc(sketch, "E13.24.8", {"start": v(33.16, -19.07) * mm, "mid": v(34.04, -19.16) * mm, "end": v(34.92, -19.16) * mm});
            skArc(sketch, "E13.24.9", {"start": v(32.86, -18.97) * mm, "mid": v(33, -19.04) * mm, "end": v(33.16, -19.07) * mm});
            skLineSegment(sketch, "E13.24.10", {"start": v(32.86, -18.97) * mm, "end": v(31.87, -18.4) * mm});
            skArc(sketch, "E13.24.11", {"start": v(31.87, -18.4) * mm, "mid": v(31.25, -18.31) * mm, "end": v(30.75, -18.69) * mm});
            skArc(sketch, "E13.25.0", {"start": v(34.96, -8.53) * mm, "mid": v(35.05, -9.15) * mm, "end": v(35.55, -9.52) * mm});
            skLineSegment(sketch, "E13.25.1", {"start": v(36.65, -9.82) * mm, "end": v(35.55, -9.52) * mm});
            skArc(sketch, "E13.25.2", {"start": v(36.93, -9.96) * mm, "mid": v(36.8, -9.88) * mm, "end": v(36.65, -9.82) * mm});
            skArc(sketch, "E13.25.3", {"start": v(36.93, -9.96) * mm, "mid": v(37.61, -10.52) * mm, "end": v(38.24, -11.15) * mm});
            skArc(sketch, "E13.25.4", {"start": v(38.43, -11.92) * mm, "mid": v(38.43, -11.5) * mm, "end": v(38.24, -11.15) * mm});
            skLineSegment(sketch, "E13.25.5", {"start": v(38.43, -11.92) * mm, "end": v(38.38, -12.1) * mm});
            skLineSegment(sketch, "E13.25.6", {"start": v(38.31, -12.28) * mm, "end": v(38.38, -12.1) * mm});
            skArc(sketch, "E13.25.7", {"start": v(37.72, -12.8) * mm, "mid": v(38.08, -12.62) * mm, "end": v(38.31, -12.28) * mm});
            skArc(sketch, "E13.25.8", {"start": v(35.97, -13.03) * mm, "mid": v(36.85, -12.95) * mm, "end": v(37.72, -12.8) * mm});
            skArc(sketch, "E13.25.9", {"start": v(35.65, -12.98) * mm, "mid": v(35.8, -13.02) * mm, "end": v(35.97, -13.03) * mm});
            skLineSegment(sketch, "E13.25.10", {"start": v(35.65, -12.98) * mm, "end": v(34.58, -12.59) * mm});
            skArc(sketch, "E13.25.11", {"start": v(34.58, -12.59) * mm, "mid": v(33.96, -12.6) * mm, "end": v(33.53, -13.06) * mm});
            skArc(sketch, "E13.26.0", {"start": v(35.9, -2.33) * mm, "mid": v(36.1, -2.92) * mm, "end": v(36.66, -3.2) * mm});
            skLineSegment(sketch, "E13.26.1", {"start": v(37.8, -3.3) * mm, "end": v(36.66, -3.2) * mm});
            skArc(sketch, "E13.26.2", {"start": v(38.1, -3.4) * mm, "mid": v(37.95, -3.34) * mm, "end": v(37.8, -3.3) * mm});
            skArc(sketch, "E13.26.3", {"start": v(38.1, -3.4) * mm, "mid": v(38.87, -3.83) * mm, "end": v(39.6, -4.34) * mm});
            skArc(sketch, "E13.26.4", {"start": v(39.91, -5.06) * mm, "mid": v(39.85, -4.66) * mm, "end": v(39.6, -4.34) * mm});
            skLineSegment(sketch, "E13.26.5", {"start": v(39.91, -5.06) * mm, "end": v(39.9, -5.25) * mm});
            skLineSegment(sketch, "E13.26.6", {"start": v(39.86, -5.44) * mm, "end": v(39.9, -5.25) * mm});
            skArc(sketch, "E13.26.7", {"start": v(39.37, -6.06) * mm, "mid": v(39.7, -5.81) * mm, "end": v(39.86, -5.44) * mm});
            skArc(sketch, "E13.26.8", {"start": v(37.68, -6.58) * mm, "mid": v(38.54, -6.36) * mm, "end": v(39.37, -6.06) * mm});
            skArc(sketch, "E13.26.9", {"start": v(37.37, -6.59) * mm, "mid": v(37.52, -6.6) * mm, "end": v(37.68, -6.58) * mm});
            skLineSegment(sketch, "E13.26.10", {"start": v(37.37, -6.59) * mm, "end": v(36.24, -6.4) * mm});
            skArc(sketch, "E13.26.11", {"start": v(36.24, -6.4) * mm, "mid": v(35.63, -6.52) * mm, "end": v(35.29, -7.04) * mm});
            skArc(sketch, "E13.27.0", {"start": v(35.77, 3.94) * mm, "mid": v(36.06, 3.4) * mm, "end": v(36.66, 3.2) * mm});
            skLineSegment(sketch, "E13.27.1", {"start": v(37.8, 3.3) * mm, "end": v(36.66, 3.2) * mm});
            skArc(sketch, "E13.27.2", {"start": v(38.11, 3.27) * mm, "mid": v(37.96, 3.3) * mm, "end": v(37.8, 3.3) * mm});
            skArc(sketch, "E13.27.3", {"start": v(38.11, 3.27) * mm, "mid": v(38.94, 2.98) * mm, "end": v(39.75, 2.6) * mm});
            skArc(sketch, "E13.27.4", {"start": v(40.18, 1.94) * mm, "mid": v(40.05, 2.33) * mm, "end": v(39.75, 2.6) * mm});
            skLineSegment(sketch, "E13.27.5", {"start": v(40.18, 1.94) * mm, "end": v(40.2, 1.76) * mm});
            skLineSegment(sketch, "E13.27.6", {"start": v(40.2, 1.57) * mm, "end": v(40.2, 1.76) * mm});
            skArc(sketch, "E13.27.7", {"start": v(39.82, 0.87) * mm, "mid": v(40.1, 1.17) * mm, "end": v(40.2, 1.57) * mm});
            skArc(sketch, "E13.27.8", {"start": v(38.25, 0.06) * mm, "mid": v(39.06, 0.43) * mm, "end": v(39.82, 0.87) * mm});
            skArc(sketch, "E13.27.9", {"start": v(37.94, 0) * mm, "mid": v(38.1, 0.02) * mm, "end": v(38.25, 0.06) * mm});
            skLineSegment(sketch, "E13.27.10", {"start": v(37.94, 0) * mm, "end": v(36.8, 0) * mm});
            skArc(sketch, "E13.27.11", {"start": v(36.8, 0) * mm, "mid": v(36.22, -0.24) * mm, "end": v(35.97, -0.8) * mm});
            skArc(sketch, "E13.28.0", {"start": v(34.54, 10.1) * mm, "mid": v(34.93, 9.6) * mm, "end": v(35.55, 9.52) * mm});
            skLineSegment(sketch, "E13.28.1", {"start": v(36.65, 9.82) * mm, "end": v(35.55, 9.52) * mm});
            skArc(sketch, "E13.28.2", {"start": v(36.96, 9.84) * mm, "mid": v(36.8, 9.85) * mm, "end": v(36.65, 9.82) * mm});
            skArc(sketch, "E13.28.3", {"start": v(36.96, 9.84) * mm, "mid": v(37.84, 9.7) * mm, "end": v(38.69, 9.47) * mm});
            skArc(sketch, "E13.28.4", {"start": v(39.24, 8.9) * mm, "mid": v(39.04, 9.25) * mm, "end": v(38.69, 9.47) * mm});
            skLineSegment(sketch, "E13.28.5", {"start": v(39.24, 8.9) * mm, "end": v(39.29, 8.7) * mm});
            skLineSegment(sketch, "E13.28.6", {"start": v(39.32, 8.52) * mm, "end": v(39.29, 8.7) * mm});
            skArc(sketch, "E13.28.7", {"start": v(39.06, 7.77) * mm, "mid": v(39.29, 8.12) * mm, "end": v(39.32, 8.52) * mm});
            skArc(sketch, "E13.28.8", {"start": v(37.66, 6.7) * mm, "mid": v(38.39, 7.2) * mm, "end": v(39.06, 7.77) * mm});
            skArc(sketch, "E13.28.9", {"start": v(37.37, 6.59) * mm, "mid": v(37.52, 6.63) * mm, "end": v(37.66, 6.7) * mm});
            skLineSegment(sketch, "E13.28.10", {"start": v(37.37, 6.59) * mm, "end": v(36.24, 6.4) * mm});
            skArc(sketch, "E13.28.11", {"start": v(36.24, 6.4) * mm, "mid": v(35.71, 6.06) * mm, "end": v(35.57, 5.45) * mm});
            skArc(sketch, "E13.29.0", {"start": v(32.26, 15.93) * mm, "mid": v(32.73, 15.52) * mm, "end": v(33.35, 15.55) * mm});
            skLineSegment(sketch, "E13.29.1", {"start": v(34.39, 16.04) * mm, "end": v(33.35, 15.55) * mm});
            skArc(sketch, "E13.29.2", {"start": v(34.7, 16.11) * mm, "mid": v(34.54, 16.09) * mm, "end": v(34.39, 16.04) * mm});
            skArc(sketch, "E13.29.3", {"start": v(34.7, 16.11) * mm, "mid": v(35.58, 16.12) * mm, "end": v(36.46, 16.04) * mm});
            skArc(sketch, "E13.29.4", {"start": v(37.1, 15.57) * mm, "mid": v(36.84, 15.89) * mm, "end": v(36.46, 16.04) * mm});
            skLineSegment(sketch, "E13.29.5", {"start": v(37.1, 15.57) * mm, "end": v(37.18, 15.4) * mm});
            skLineSegment(sketch, "E13.29.6", {"start": v(37.24, 15.22) * mm, "end": v(37.18, 15.4) * mm});
            skArc(sketch, "E13.29.7", {"start": v(37.12, 14.44) * mm, "mid": v(37.28, 14.81) * mm, "end": v(37.24, 15.22) * mm});
            skArc(sketch, "E13.29.8", {"start": v(35.93, 13.14) * mm, "mid": v(36.55, 13.76) * mm, "end": v(37.12, 14.44) * mm});
            skArc(sketch, "E13.29.9", {"start": v(35.65, 12.98) * mm, "mid": v(35.8, 13.05) * mm, "end": v(35.93, 13.14) * mm});
            skLineSegment(sketch, "E13.29.10", {"start": v(35.65, 12.98) * mm, "end": v(34.58, 12.59) * mm});
            skArc(sketch, "E13.29.11", {"start": v(34.58, 12.59) * mm, "mid": v(34.12, 12.17) * mm, "end": v(34.08, 11.55) * mm});
            skArc(sketch, "E13.30.0", {"start": v(29, 21.3) * mm, "mid": v(29.54, 20.97) * mm, "end": v(30.14, 21.1) * mm});
            skLineSegment(sketch, "E13.30.1", {"start": v(31.08, 21.76) * mm, "end": v(30.14, 21.1) * mm});
            skArc(sketch, "E13.30.2", {"start": v(31.37, 21.9) * mm, "mid": v(31.22, 21.84) * mm, "end": v(31.08, 21.76) * mm});
            skArc(sketch, "E13.30.3", {"start": v(31.37, 21.9) * mm, "mid": v(32.24, 22.05) * mm, "end": v(33.12, 22.13) * mm});
            skArc(sketch, "E13.30.4", {"start": v(33.83, 21.78) * mm, "mid": v(33.52, 22.04) * mm, "end": v(33.12, 22.13) * mm});
            skLineSegment(sketch, "E13.30.5", {"start": v(33.83, 21.78) * mm, "end": v(33.94, 21.62) * mm});
            skLineSegment(sketch, "E13.30.6", {"start": v(34.03, 21.46) * mm, "end": v(33.94, 21.62) * mm});
            skArc(sketch, "E13.30.7", {"start": v(34.05, 20.66) * mm, "mid": v(34.14, 21.06) * mm, "end": v(34.03, 21.46) * mm});
            skArc(sketch, "E13.30.8", {"start": v(33.1, 19.18) * mm, "mid": v(33.6, 19.9) * mm, "end": v(34.05, 20.66) * mm});
            skArc(sketch, "E13.30.9", {"start": v(32.86, 18.97) * mm, "mid": v(32.99, 19.06) * mm, "end": v(33.1, 19.18) * mm});
            skLineSegment(sketch, "E13.30.10", {"start": v(32.86, 18.97) * mm, "end": v(31.87, 18.4) * mm});
            skArc(sketch, "E13.30.11", {"start": v(31.87, 18.4) * mm, "mid": v(31.49, 17.9) * mm, "end": v(31.56, 17.29) * mm});
            skArc(sketch, "E13.31.0", {"start": v(24.87, 26) * mm, "mid": v(25.45, 25.78) * mm, "end": v(26.02, 26.02) * mm});
            skLineSegment(sketch, "E13.31.1", {"start": v(26.83, 26.83) * mm, "end": v(26.02, 26.02) * mm});
            skArc(sketch, "E13.31.2", {"start": v(27.1, 27) * mm, "mid": v(26.95, 26.93) * mm, "end": v(26.83, 26.83) * mm});
            skArc(sketch, "E13.31.3", {"start": v(27.1, 27) * mm, "mid": v(27.92, 27.31) * mm, "end": v(28.77, 27.54) * mm});
            skArc(sketch, "E13.31.4", {"start": v(29.53, 27.32) * mm, "mid": v(29.18, 27.53) * mm, "end": v(28.77, 27.54) * mm});
            skLineSegment(sketch, "E13.31.5", {"start": v(29.53, 27.32) * mm, "end": v(29.67, 27.19) * mm});
            skLineSegment(sketch, "E13.31.6", {"start": v(29.79, 27.04) * mm, "end": v(29.67, 27.19) * mm});
            skArc(sketch, "E13.31.7", {"start": v(29.94, 26.26) * mm, "mid": v(29.97, 26.67) * mm, "end": v(29.79, 27.04) * mm});
            skArc(sketch, "E13.31.8", {"start": v(29.26, 24.63) * mm, "mid": v(29.64, 25.43) * mm, "end": v(29.94, 26.26) * mm});
            skArc(sketch, "E13.31.9", {"start": v(29.07, 24.39) * mm, "mid": v(29.18, 24.5) * mm, "end": v(29.26, 24.63) * mm});
            skLineSegment(sketch, "E13.31.10", {"start": v(29.07, 24.39) * mm, "end": v(28.2, 23.65) * mm});
            skArc(sketch, "E13.31.11", {"start": v(28.2, 23.65) * mm, "mid": v(27.9, 23.1) * mm, "end": v(28.08, 22.5) * mm});
            skArc(sketch, "E13.32.0", {"start": v(19.97, 29.93) * mm, "mid": v(20.58, 29.8) * mm, "end": v(21.1, 30.14) * mm});
            skLineSegment(sketch, "E13.32.1", {"start": v(21.76, 31.08) * mm, "end": v(21.1, 30.14) * mm});
            skArc(sketch, "E13.32.2", {"start": v(22, 31.3) * mm, "mid": v(21.87, 31.2) * mm, "end": v(21.76, 31.08) * mm});
            skArc(sketch, "E13.32.3", {"start": v(22, 31.3) * mm, "mid": v(22.75, 31.75) * mm, "end": v(23.55, 32.12) * mm});
            skArc(sketch, "E13.32.4", {"start": v(24.34, 32.03) * mm, "mid": v(23.96, 32.18) * mm, "end": v(23.55, 32.12) * mm});
            skLineSegment(sketch, "E13.32.5", {"start": v(24.34, 32.03) * mm, "end": v(24.5, 31.92) * mm});
            skLineSegment(sketch, "E13.32.6", {"start": v(24.64, 31.8) * mm, "end": v(24.5, 31.92) * mm});
            skArc(sketch, "E13.32.7", {"start": v(24.93, 31.06) * mm, "mid": v(24.88, 31.47) * mm, "end": v(24.64, 31.8) * mm});
            skArc(sketch, "E13.32.8", {"start": v(24.54, 29.34) * mm, "mid": v(24.78, 30.2) * mm, "end": v(24.93, 31.06) * mm});
            skArc(sketch, "E13.32.9", {"start": v(24.39, 29.07) * mm, "mid": v(24.48, 29.2) * mm, "end": v(24.54, 29.34) * mm});
            skLineSegment(sketch, "E13.32.10", {"start": v(24.39, 29.07) * mm, "end": v(23.65, 28.2) * mm});
            skArc(sketch, "E13.32.11", {"start": v(23.65, 28.2) * mm, "mid": v(23.46, 27.6) * mm, "end": v(23.74, 27.04) * mm});
            skArc(sketch, "E13.33.0", {"start": v(14.47, 32.94) * mm, "mid": v(15.1, 32.93) * mm, "end": v(15.55, 33.35) * mm});
            skLineSegment(sketch, "E13.33.1", {"start": v(16.04, 34.39) * mm, "end": v(15.55, 33.35) * mm});
            skArc(sketch, "E13.33.2", {"start": v(16.22, 34.64) * mm, "mid": v(16.12, 34.52) * mm, "end": v(16.04, 34.39) * mm});
            skArc(sketch, "E13.33.3", {"start": v(16.22, 34.64) * mm, "mid": v(16.9, 35.21) * mm, "end": v(17.62, 35.72) * mm});
            skArc(sketch, "E13.33.4", {"start": v(18.4, 35.77) * mm, "mid": v(18, 35.85) * mm, "end": v(17.62, 35.72) * mm});
            skLineSegment(sketch, "E13.33.5", {"start": v(18.4, 35.77) * mm, "end": v(18.58, 35.7) * mm});
            skLineSegment(sketch, "E13.33.6", {"start": v(18.74, 35.6) * mm, "end": v(18.58, 35.7) * mm});
            skArc(sketch, "E13.33.7", {"start": v(19.16, 34.92) * mm, "mid": v(19.04, 35.31) * mm, "end": v(18.74, 35.6) * mm});
            skArc(sketch, "E13.33.8", {"start": v(19.07, 33.16) * mm, "mid": v(19.16, 34.04) * mm, "end": v(19.16, 34.92) * mm});
            skArc(sketch, "E13.33.9", {"start": v(18.97, 32.86) * mm, "mid": v(19.04, 33) * mm, "end": v(19.07, 33.16) * mm});
            skLineSegment(sketch, "E13.33.10", {"start": v(18.97, 32.86) * mm, "end": v(18.4, 31.87) * mm});
            skArc(sketch, "E13.33.11", {"start": v(18.4, 31.87) * mm, "mid": v(18.31, 31.25) * mm, "end": v(18.69, 30.75) * mm});
            skArc(sketch, "E13.34.0", {"start": v(8.53, 34.96) * mm, "mid": v(9.15, 35.05) * mm, "end": v(9.52, 35.55) * mm});
            skLineSegment(sketch, "E13.34.1", {"start": v(9.82, 36.65) * mm, "end": v(9.52, 35.55) * mm});
            skArc(sketch, "E13.34.2", {"start": v(9.96, 36.93) * mm, "mid": v(9.88, 36.8) * mm, "end": v(9.82, 36.65) * mm});
            skArc(sketch, "E13.34.3", {"start": v(9.96, 36.93) * mm, "mid": v(10.52, 37.61) * mm, "end": v(11.15, 38.24) * mm});
            skArc(sketch, "E13.34.4", {"start": v(11.92, 38.43) * mm, "mid": v(11.5, 38.43) * mm, "end": v(11.15, 38.24) * mm});
            skLineSegment(sketch, "E13.34.5", {"start": v(11.92, 38.43) * mm, "end": v(12.1, 38.38) * mm});
            skLineSegment(sketch, "E13.34.6", {"start": v(12.28, 38.31) * mm, "end": v(12.1, 38.38) * mm});
            skArc(sketch, "E13.34.7", {"start": v(12.8, 37.72) * mm, "mid": v(12.62, 38.08) * mm, "end": v(12.28, 38.31) * mm});
            skArc(sketch, "E13.34.8", {"start": v(13.03, 35.97) * mm, "mid": v(12.95, 36.85) * mm, "end": v(12.8, 37.72) * mm});
            skArc(sketch, "E13.34.9", {"start": v(12.98, 35.65) * mm, "mid": v(13.02, 35.8) * mm, "end": v(13.03, 35.97) * mm});
            skLineSegment(sketch, "E13.34.10", {"start": v(12.98, 35.65) * mm, "end": v(12.59, 34.58) * mm});
            skArc(sketch, "E13.34.11", {"start": v(12.59, 34.58) * mm, "mid": v(12.6, 33.96) * mm, "end": v(13.06, 33.53) * mm});
            skArc(sketch, "E13.35.0", {"start": v(2.33, 35.9) * mm, "mid": v(2.92, 36.1) * mm, "end": v(3.2, 36.66) * mm});
            skLineSegment(sketch, "E13.35.1", {"start": v(3.3, 37.8) * mm, "end": v(3.2, 36.66) * mm});
            skArc(sketch, "E13.35.2", {"start": v(3.4, 38.1) * mm, "mid": v(3.34, 37.95) * mm, "end": v(3.3, 37.8) * mm});
            skArc(sketch, "E13.35.3", {"start": v(3.4, 38.1) * mm, "mid": v(3.83, 38.87) * mm, "end": v(4.34, 39.6) * mm});
            skArc(sketch, "E13.35.4", {"start": v(5.06, 39.91) * mm, "mid": v(4.66, 39.85) * mm, "end": v(4.34, 39.6) * mm});
            skLineSegment(sketch, "E13.35.5", {"start": v(5.06, 39.91) * mm, "end": v(5.25, 39.9) * mm});
            skLineSegment(sketch, "E13.35.6", {"start": v(5.44, 39.86) * mm, "end": v(5.25, 39.9) * mm});
            skArc(sketch, "E13.35.7", {"start": v(6.06, 39.37) * mm, "mid": v(5.81, 39.7) * mm, "end": v(5.44, 39.86) * mm});
            skArc(sketch, "E13.35.8", {"start": v(6.58, 37.68) * mm, "mid": v(6.36, 38.54) * mm, "end": v(6.06, 39.37) * mm});
            skArc(sketch, "E13.35.9", {"start": v(6.59, 37.37) * mm, "mid": v(6.6, 37.52) * mm, "end": v(6.58, 37.68) * mm});
            skLineSegment(sketch, "E13.35.10", {"start": v(6.59, 37.37) * mm, "end": v(6.4, 36.24) * mm});
            skArc(sketch, "E13.35.11", {"start": v(6.4, 36.24) * mm, "mid": v(6.52, 35.63) * mm, "end": v(7.04, 35.29) * mm});
            skArc(sketch, "E14.trimOffspring", {"start": v(-10.1, 34.54) * mm, "mid": v(-10.82, 34.32) * mm, "end": v(-11.55, 34.08) * mm});
            skArc(sketch, "E15.trimOffspring", {"start": v(-15.93, 32.26) * mm, "mid": v(-16.62, 31.92) * mm, "end": v(-17.29, 31.56) * mm});
            skArc(sketch, "E16.trimOffspring", {"start": v(-21.3, 29) * mm, "mid": v(-21.9, 28.55) * mm, "end": v(-22.5, 28.08) * mm});
            skArc(sketch, "E17.trimOffspring", {"start": v(-26, 24.87) * mm, "mid": v(-26.53, 24.3) * mm, "end": v(-27.04, 23.74) * mm});
            skArc(sketch, "E18.trimOffspring", {"start": v(-29.93, 19.97) * mm, "mid": v(-30.35, 19.33) * mm, "end": v(-30.75, 18.69) * mm});
            skArc(sketch, "E19.trimOffspring", {"start": v(-32.94, 14.47) * mm, "mid": v(-33.24, 13.77) * mm, "end": v(-33.53, 13.06) * mm});
            skArc(sketch, "E20.trimOffspring", {"start": v(-34.96, 8.53) * mm, "mid": v(-35.13, 7.79) * mm, "end": v(-35.29, 7.04) * mm});
            skArc(sketch, "E21.trimOffspring", {"start": v(2.33, 35.9) * mm, "mid": v(1.57, 35.95) * mm, "end": v(0.8, 35.97) * mm});
            skArc(sketch, "E22.trimOffspring", {"start": v(14.47, 32.94) * mm, "mid": v(13.77, 33.24) * mm, "end": v(13.06, 33.53) * mm});
            skArc(sketch, "E23.trimOffspring", {"start": v(19.97, 29.93) * mm, "mid": v(19.33, 30.35) * mm, "end": v(18.69, 30.75) * mm});
            skArc(sketch, "E24.trimOffspring", {"start": v(8.53, 34.96) * mm, "mid": v(7.79, 35.13) * mm, "end": v(7.04, 35.29) * mm});
            skArc(sketch, "E25.trimOffspring", {"start": v(24.87, 26) * mm, "mid": v(24.3, 26.53) * mm, "end": v(23.74, 27.04) * mm});
            skArc(sketch, "E26.trimOffspring", {"start": v(29, 21.3) * mm, "mid": v(28.55, 21.9) * mm, "end": v(28.08, 22.5) * mm});
            skArc(sketch, "E27.trimOffspring", {"start": v(-35.9, 2.33) * mm, "mid": v(-35.95, 1.57) * mm, "end": v(-35.97, 0.8) * mm});
            skArc(sketch, "E28.trimOffspring", {"start": v(-35.77, -3.94) * mm, "mid": v(-35.68, -4.7) * mm, "end": v(-35.57, -5.45) * mm});
            skArc(sketch, "E29.trimOffspring", {"start": v(-34.54, -10.1) * mm, "mid": v(-34.32, -10.82) * mm, "end": v(-34.08, -11.55) * mm});
            skArc(sketch, "E30.trimOffspring", {"start": v(-32.26, -15.93) * mm, "mid": v(-31.92, -16.62) * mm, "end": v(-31.56, -17.29) * mm});
            skArc(sketch, "E31.trimOffspring", {"start": v(-29, -21.3) * mm, "mid": v(-28.55, -21.9) * mm, "end": v(-28.08, -22.5) * mm});
            skArc(sketch, "E32.trimOffspring", {"start": v(-24.87, -26) * mm, "mid": v(-24.3, -26.53) * mm, "end": v(-23.74, -27.04) * mm});
            skArc(sketch, "E33.trimOffspring", {"start": v(-19.97, -29.93) * mm, "mid": v(-19.33, -30.35) * mm, "end": v(-18.69, -30.75) * mm});
            skArc(sketch, "E34.trimOffspring", {"start": v(-14.47, -32.94) * mm, "mid": v(-13.77, -33.24) * mm, "end": v(-13.06, -33.53) * mm});
            skArc(sketch, "E35.trimOffspring", {"start": v(-8.53, -34.96) * mm, "mid": v(-7.79, -35.13) * mm, "end": v(-7.04, -35.29) * mm});
            skArc(sketch, "E36.trimOffspring", {"start": v(-2.33, -35.9) * mm, "mid": v(-1.57, -35.95) * mm, "end": v(-0.8, -35.97) * mm});
            skArc(sketch, "E37.trimOffspring", {"start": v(3.94, -35.77) * mm, "mid": v(4.7, -35.68) * mm, "end": v(5.45, -35.57) * mm});
            skArc(sketch, "E38.trimOffspring", {"start": v(10.1, -34.54) * mm, "mid": v(10.82, -34.32) * mm, "end": v(11.55, -34.08) * mm});
            skArc(sketch, "E39.trimOffspring", {"start": v(15.93, -32.26) * mm, "mid": v(16.62, -31.92) * mm, "end": v(17.29, -31.56) * mm});
            skArc(sketch, "E40.trimOffspring", {"start": v(21.3, -29) * mm, "mid": v(21.9, -28.55) * mm, "end": v(22.5, -28.08) * mm});
            skArc(sketch, "E41.trimOffspring", {"start": v(26, -24.87) * mm, "mid": v(26.53, -24.3) * mm, "end": v(27.04, -23.74) * mm});
            skArc(sketch, "E42.trimOffspring", {"start": v(29.93, -19.97) * mm, "mid": v(30.35, -19.33) * mm, "end": v(30.75, -18.69) * mm});
            skArc(sketch, "E43.trimOffspring", {"start": v(32.94, -14.47) * mm, "mid": v(33.24, -13.77) * mm, "end": v(33.53, -13.06) * mm});
            skArc(sketch, "E44.trimOffspring", {"start": v(34.96, -8.53) * mm, "mid": v(35.13, -7.79) * mm, "end": v(35.29, -7.04) * mm});
            skArc(sketch, "E45.trimOffspring", {"start": v(35.9, -2.33) * mm, "mid": v(35.95, -1.57) * mm, "end": v(35.97, -0.8) * mm});
            skArc(sketch, "E46.trimOffspring", {"start": v(32.26, 15.93) * mm, "mid": v(31.92, 16.62) * mm, "end": v(31.56, 17.29) * mm});
            skArc(sketch, "E47.trimOffspring", {"start": v(34.54, 10.1) * mm, "mid": v(34.32, 10.82) * mm, "end": v(34.08, 11.55) * mm});
            skArc(sketch, "E48.trimOffspring", {"start": v(35.77, 3.94) * mm, "mid": v(35.68, 4.7) * mm, "end": v(35.57, 5.45) * mm});
            skSolve(sketch);
        }
        {
            var Q0;
            Q0=qSketchRegion(id+"F0",true);
            extrude(context, id + "F1", {"entities" : qUnion([Q0]), "depth" : 12.7 * mm});
        }
        {
            var Q0;
            Q0=makeQuery(id+"F1.opExtrude","CAP_FACE",FACE,{"disambiguationData":[OSD([sQuery(id+"F0.wireOp",EDGE,"E0"),sQuery(id+"F0.wireOp",EDGE,"E1"),sQuery(id+"F0.wireOp",EDGE,"E2"),sQuery(id+"F0.wireOp",EDGE,"E3.trimOffspring"),sQuery(id+"F0.wireOp",EDGE,"E4.MirrorCS"),sQuery(id+"F0.wireOp",EDGE,"E5.MirrorCS"),sQuery(id+"F0.wireOp",EDGE,"E6.MirrorCS"),sQuery(id+"F0.wireOp",EDGE,"E7.filletArc"),sQuery(id+"F0.wireOp",EDGE,"E8.filletArc"),sQuery(id+"F0.wireOp",EDGE,"E9.filletArc"),sQuery(id+"F0.wireOp",EDGE,"E10.filletArc"),sQuery(id+"F0.wireOp",EDGE,"E11.filletArc"),sQuery(id+"F0.wireOp",EDGE,"E12.filletArc"),sQuery(id+"F0.wireOp",EDGE,"E13.1.0"),sQuery(id+"F0.wireOp",EDGE,"E13.1.1"),sQuery(id+"F0.wireOp",EDGE,"E13.1.2"),sQuery(id+"F0.wireOp",EDGE,"E13.1.3"),sQuery(id+"F0.wireOp",EDGE,"E13.1.4"),sQuery(id+"F0.wireOp",EDGE,"E13.1.5"),sQuery(id+"F0.wireOp",EDGE,"E13.1.6"),sQuery(id+"F0.wireOp",EDGE,"E13.1.7"),sQuery(id+"F0.wireOp",EDGE,"E13.1.8"),sQuery(id+"F0.wireOp",EDGE,"E13.1.9"),sQuery(id+"F0.wireOp",EDGE,"E13.1.10"),sQuery(id+"F0.wireOp",EDGE,"E13.1.11"),sQuery(id+"F0.wireOp",EDGE,"E13.2.0"),sQuery(id+"F0.wireOp",EDGE,"E13.2.1"),sQuery(id+"F0.wireOp",EDGE,"E13.2.2"),sQuery(id+"F0.wireOp",EDGE,"E13.2.3"),sQuery(id+"F0.wireOp",EDGE,"E13.2.4"),sQuery(id+"F0.wireOp",EDGE,"E13.2.5"),sQuery(id+"F0.wireOp",EDGE,"E13.2.6"),sQuery(id+"F0.wireOp",EDGE,"E13.2.7"),sQuery(id+"F0.wireOp",EDGE,"E13.2.8"),sQuery(id+"F0.wireOp",EDGE,"E13.2.9"),sQuery(id+"F0.wireOp",EDGE,"E13.2.10"),sQuery(id+"F0.wireOp",EDGE,"E13.2.11"),sQuery(id+"F0.wireOp",EDGE,"E13.3.0"),sQuery(id+"F0.wireOp",EDGE,"E13.3.1"),sQuery(id+"F0.wireOp",EDGE,"E13.3.2"),sQuery(id+"F0.wireOp",EDGE,"E13.3.3"),sQuery(id+"F0.wireOp",EDGE,"E13.3.4"),sQuery(id+"F0.wireOp",EDGE,"E13.3.5"),sQuery(id+"F0.wireOp",EDGE,"E13.3.6"),sQuery(id+"F0.wireOp",EDGE,"E13.3.7"),sQuery(id+"F0.wireOp",EDGE,"E13.3.8"),sQuery(id+"F0.wireOp",EDGE,"E13.3.9"),sQuery(id+"F0.wireOp",EDGE,"E13.3.10"),sQuery(id+"F0.wireOp",EDGE,"E13.3.11"),sQuery(id+"F0.wireOp",EDGE,"E13.4.0"),sQuery(id+"F0.wireOp",EDGE,"E13.4.1"),sQuery(id+"F0.wireOp",EDGE,"E13.4.2"),sQuery(id+"F0.wireOp",EDGE,"E13.4.3"),sQuery(id+"F0.wireOp",EDGE,"E13.4.4"),sQuery(id+"F0.wireOp",EDGE,"E13.4.5"),sQuery(id+"F0.wireOp",EDGE,"E13.4.6"),sQuery(id+"F0.wireOp",EDGE,"E13.4.7"),sQuery(id+"F0.wireOp",EDGE,"E13.4.8"),sQuery(id+"F0.wireOp",EDGE,"E13.4.9"),sQuery(id+"F0.wireOp",EDGE,"E13.4.10"),sQuery(id+"F0.wireOp",EDGE,"E13.4.11"),sQuery(id+"F0.wireOp",EDGE,"E13.5.0"),sQuery(id+"F0.wireOp",EDGE,"E13.5.1"),sQuery(id+"F0.wireOp",EDGE,"E13.5.2"),sQuery(id+"F0.wireOp",EDGE,"E13.5.3"),sQuery(id+"F0.wireOp",EDGE,"E13.5.4"),sQuery(id+"F0.wireOp",EDGE,"E13.5.5"),sQuery(id+"F0.wireOp",EDGE,"E13.5.6"),sQuery(id+"F0.wireOp",EDGE,"E13.5.7"),sQuery(id+"F0.wireOp",EDGE,"E13.5.8"),sQuery(id+"F0.wireOp",EDGE,"E13.5.9"),sQuery(id+"F0.wireOp",EDGE,"E13.5.10"),sQuery(id+"F0.wireOp",EDGE,"E13.5.11"),sQuery(id+"F0.wireOp",EDGE,"E13.6.0"),sQuery(id+"F0.wireOp",EDGE,"E13.6.1"),sQuery(id+"F0.wireOp",EDGE,"E13.6.2"),sQuery(id+"F0.wireOp",EDGE,"E13.6.3"),sQuery(id+"F0.wireOp",EDGE,"E13.6.4"),sQuery(id+"F0.wireOp",EDGE,"E13.6.5"),sQuery(id+"F0.wireOp",EDGE,"E13.6.6"),sQuery(id+"F0.wireOp",EDGE,"E13.6.7"),sQuery(id+"F0.wireOp",EDGE,"E13.6.8"),sQuery(id+"F0.wireOp",EDGE,"E13.6.9"),sQuery(id+"F0.wireOp",EDGE,"E13.6.10"),sQuery(id+"F0.wireOp",EDGE,"E13.6.11"),sQuery(id+"F0.wireOp",EDGE,"E13.7.0"),sQuery(id+"F0.wireOp",EDGE,"E13.7.1"),sQuery(id+"F0.wireOp",EDGE,"E13.7.2"),sQuery(id+"F0.wireOp",EDGE,"E13.7.3"),sQuery(id+"F0.wireOp",EDGE,"E13.7.4"),sQuery(id+"F0.wireOp",EDGE,"E13.7.5"),sQuery(id+"F0.wireOp",EDGE,"E13.7.6"),sQuery(id+"F0.wireOp",EDGE,"E13.7.7"),sQuery(id+"F0.wireOp",EDGE,"E13.7.8"),sQuery(id+"F0.wireOp",EDGE,"E13.7.9"),sQuery(id+"F0.wireOp",EDGE,"E13.7.10"),sQuery(id+"F0.wireOp",EDGE,"E13.7.11"),sQuery(id+"F0.wireOp",EDGE,"E13.8.0"),sQuery(id+"F0.wireOp",EDGE,"E13.8.1"),sQuery(id+"F0.wireOp",EDGE,"E13.8.2"),sQuery(id+"F0.wireOp",EDGE,"E13.8.3"),sQuery(id+"F0.wireOp",EDGE,"E13.8.4"),sQuery(id+"F0.wireOp",EDGE,"E13.8.5"),sQuery(id+"F0.wireOp",EDGE,"E13.8.6"),sQuery(id+"F0.wireOp",EDGE,"E13.8.7"),sQuery(id+"F0.wireOp",EDGE,"E13.8.8"),sQuery(id+"F0.wireOp",EDGE,"E13.8.9"),sQuery(id+"F0.wireOp",EDGE,"E13.8.10"),sQuery(id+"F0.wireOp",EDGE,"E13.8.11"),sQuery(id+"F0.wireOp",EDGE,"E13.9.0"),sQuery(id+"F0.wireOp",EDGE,"E13.9.1"),sQuery(id+"F0.wireOp",EDGE,"E13.9.2"),sQuery(id+"F0.wireOp",EDGE,"E13.9.3"),sQuery(id+"F0.wireOp",EDGE,"E13.9.4"),sQuery(id+"F0.wireOp",EDGE,"E13.9.5"),sQuery(id+"F0.wireOp",EDGE,"E13.9.6"),sQuery(id+"F0.wireOp",EDGE,"E13.9.7"),sQuery(id+"F0.wireOp",EDGE,"E13.9.8"),sQuery(id+"F0.wireOp",EDGE,"E13.9.9"),sQuery(id+"F0.wireOp",EDGE,"E13.9.10"),sQuery(id+"F0.wireOp",EDGE,"E13.9.11"),sQuery(id+"F0.wireOp",EDGE,"E13.10.0"),sQuery(id+"F0.wireOp",EDGE,"E13.10.1"),sQuery(id+"F0.wireOp",EDGE,"E13.10.2"),sQuery(id+"F0.wireOp",EDGE,"E13.10.3"),sQuery(id+"F0.wireOp",EDGE,"E13.10.4"),sQuery(id+"F0.wireOp",EDGE,"E13.10.5"),sQuery(id+"F0.wireOp",EDGE,"E13.10.6"),sQuery(id+"F0.wireOp",EDGE,"E13.10.7"),sQuery(id+"F0.wireOp",EDGE,"E13.10.8"),sQuery(id+"F0.wireOp",EDGE,"E13.10.9"),sQuery(id+"F0.wireOp",EDGE,"E13.10.10"),sQuery(id+"F0.wireOp",EDGE,"E13.10.11"),sQuery(id+"F0.wireOp",EDGE,"E13.11.0"),sQuery(id+"F0.wireOp",EDGE,"E13.11.1"),sQuery(id+"F0.wireOp",EDGE,"E13.11.2"),sQuery(id+"F0.wireOp",EDGE,"E13.11.3"),sQuery(id+"F0.wireOp",EDGE,"E13.11.4"),sQuery(id+"F0.wireOp",EDGE,"E13.11.5"),sQuery(id+"F0.wireOp",EDGE,"E13.11.6"),sQuery(id+"F0.wireOp",EDGE,"E13.11.7"),sQuery(id+"F0.wireOp",EDGE,"E13.11.8"),sQuery(id+"F0.wireOp",EDGE,"E13.11.9"),sQuery(id+"F0.wireOp",EDGE,"E13.11.10"),sQuery(id+"F0.wireOp",EDGE,"E13.11.11"),sQuery(id+"F0.wireOp",EDGE,"E13.12.0"),sQuery(id+"F0.wireOp",EDGE,"E13.12.1"),sQuery(id+"F0.wireOp",EDGE,"E13.12.2"),sQuery(id+"F0.wireOp",EDGE,"E13.12.3"),sQuery(id+"F0.wireOp",EDGE,"E13.12.4"),sQuery(id+"F0.wireOp",EDGE,"E13.12.5"),sQuery(id+"F0.wireOp",EDGE,"E13.12.6"),sQuery(id+"F0.wireOp",EDGE,"E13.12.7"),sQuery(id+"F0.wireOp",EDGE,"E13.12.8"),sQuery(id+"F0.wireOp",EDGE,"E13.12.9"),sQuery(id+"F0.wireOp",EDGE,"E13.12.10"),sQuery(id+"F0.wireOp",EDGE,"E13.12.11"),sQuery(id+"F0.wireOp",EDGE,"E13.13.0"),sQuery(id+"F0.wireOp",EDGE,"E13.13.1"),sQuery(id+"F0.wireOp",EDGE,"E13.13.2"),sQuery(id+"F0.wireOp",EDGE,"E13.13.3"),sQuery(id+"F0.wireOp",EDGE,"E13.13.4"),sQuery(id+"F0.wireOp",EDGE,"E13.13.5"),sQuery(id+"F0.wireOp",EDGE,"E13.13.6"),sQuery(id+"F0.wireOp",EDGE,"E13.13.7"),sQuery(id+"F0.wireOp",EDGE,"E13.13.8"),sQuery(id+"F0.wireOp",EDGE,"E13.13.9"),sQuery(id+"F0.wireOp",EDGE,"E13.13.10"),sQuery(id+"F0.wireOp",EDGE,"E13.13.11"),sQuery(id+"F0.wireOp",EDGE,"E13.14.0"),sQuery(id+"F0.wireOp",EDGE,"E13.14.1"),sQuery(id+"F0.wireOp",EDGE,"E13.14.2"),sQuery(id+"F0.wireOp",EDGE,"E13.14.3"),sQuery(id+"F0.wireOp",EDGE,"E13.14.4"),sQuery(id+"F0.wireOp",EDGE,"E13.14.5"),sQuery(id+"F0.wireOp",EDGE,"E13.14.6"),sQuery(id+"F0.wireOp",EDGE,"E13.14.7"),sQuery(id+"F0.wireOp",EDGE,"E13.14.8"),sQuery(id+"F0.wireOp",EDGE,"E13.14.9"),sQuery(id+"F0.wireOp",EDGE,"E13.14.10"),sQuery(id+"F0.wireOp",EDGE,"E13.14.11"),sQuery(id+"F0.wireOp",EDGE,"E13.15.0"),sQuery(id+"F0.wireOp",EDGE,"E13.15.1"),sQuery(id+"F0.wireOp",EDGE,"E13.15.2"),sQuery(id+"F0.wireOp",EDGE,"E13.15.3"),sQuery(id+"F0.wireOp",EDGE,"E13.15.4"),sQuery(id+"F0.wireOp",EDGE,"E13.15.5"),sQuery(id+"F0.wireOp",EDGE,"E13.15.6"),sQuery(id+"F0.wireOp",EDGE,"E13.15.7"),sQuery(id+"F0.wireOp",EDGE,"E13.15.8"),sQuery(id+"F0.wireOp",EDGE,"E13.15.9"),sQuery(id+"F0.wireOp",EDGE,"E13.15.10"),sQuery(id+"F0.wireOp",EDGE,"E13.15.11"),sQuery(id+"F0.wireOp",EDGE,"E13.16.0"),sQuery(id+"F0.wireOp",EDGE,"E13.16.1"),sQuery(id+"F0.wireOp",EDGE,"E13.16.2"),sQuery(id+"F0.wireOp",EDGE,"E13.16.3"),sQuery(id+"F0.wireOp",EDGE,"E13.16.4"),sQuery(id+"F0.wireOp",EDGE,"E13.16.5"),sQuery(id+"F0.wireOp",EDGE,"E13.16.6"),sQuery(id+"F0.wireOp",EDGE,"E13.16.7"),sQuery(id+"F0.wireOp",EDGE,"E13.16.8"),sQuery(id+"F0.wireOp",EDGE,"E13.16.9"),sQuery(id+"F0.wireOp",EDGE,"E13.16.10"),sQuery(id+"F0.wireOp",EDGE,"E13.16.11"),sQuery(id+"F0.wireOp",EDGE,"E13.17.0"),sQuery(id+"F0.wireOp",EDGE,"E13.17.1"),sQuery(id+"F0.wireOp",EDGE,"E13.17.2"),sQuery(id+"F0.wireOp",EDGE,"E13.17.3"),sQuery(id+"F0.wireOp",EDGE,"E13.17.4"),sQuery(id+"F0.wireOp",EDGE,"E13.17.5"),sQuery(id+"F0.wireOp",EDGE,"E13.17.6"),sQuery(id+"F0.wireOp",EDGE,"E13.17.7"),sQuery(id+"F0.wireOp",EDGE,"E13.17.8"),sQuery(id+"F0.wireOp",EDGE,"E13.17.9"),sQuery(id+"F0.wireOp",EDGE,"E13.17.10"),sQuery(id+"F0.wireOp",EDGE,"E13.17.11"),sQuery(id+"F0.wireOp",EDGE,"E13.18.0"),sQuery(id+"F0.wireOp",EDGE,"E13.18.1"),sQuery(id+"F0.wireOp",EDGE,"E13.18.2"),sQuery(id+"F0.wireOp",EDGE,"E13.18.3"),sQuery(id+"F0.wireOp",EDGE,"E13.18.4"),sQuery(id+"F0.wireOp",EDGE,"E13.18.5"),sQuery(id+"F0.wireOp",EDGE,"E13.18.6"),sQuery(id+"F0.wireOp",EDGE,"E13.18.7"),sQuery(id+"F0.wireOp",EDGE,"E13.18.8"),sQuery(id+"F0.wireOp",EDGE,"E13.18.9"),sQuery(id+"F0.wireOp",EDGE,"E13.18.10"),sQuery(id+"F0.wireOp",EDGE,"E13.18.11"),sQuery(id+"F0.wireOp",EDGE,"E13.19.0"),sQuery(id+"F0.wireOp",EDGE,"E13.19.1"),sQuery(id+"F0.wireOp",EDGE,"E13.19.2"),sQuery(id+"F0.wireOp",EDGE,"E13.19.3"),sQuery(id+"F0.wireOp",EDGE,"E13.19.4"),sQuery(id+"F0.wireOp",EDGE,"E13.19.5"),sQuery(id+"F0.wireOp",EDGE,"E13.19.6"),sQuery(id+"F0.wireOp",EDGE,"E13.19.7"),sQuery(id+"F0.wireOp",EDGE,"E13.19.8"),sQuery(id+"F0.wireOp",EDGE,"E13.19.9"),sQuery(id+"F0.wireOp",EDGE,"E13.19.10"),sQuery(id+"F0.wireOp",EDGE,"E13.19.11"),sQuery(id+"F0.wireOp",EDGE,"E13.20.0"),sQuery(id+"F0.wireOp",EDGE,"E13.20.1"),sQuery(id+"F0.wireOp",EDGE,"E13.20.2"),sQuery(id+"F0.wireOp",EDGE,"E13.20.3"),sQuery(id+"F0.wireOp",EDGE,"E13.20.4"),sQuery(id+"F0.wireOp",EDGE,"E13.20.5"),sQuery(id+"F0.wireOp",EDGE,"E13.20.6"),sQuery(id+"F0.wireOp",EDGE,"E13.20.7"),sQuery(id+"F0.wireOp",EDGE,"E13.20.8"),sQuery(id+"F0.wireOp",EDGE,"E13.20.9"),sQuery(id+"F0.wireOp",EDGE,"E13.20.10"),sQuery(id+"F0.wireOp",EDGE,"E13.20.11"),sQuery(id+"F0.wireOp",EDGE,"E13.21.0"),sQuery(id+"F0.wireOp",EDGE,"E13.21.1"),sQuery(id+"F0.wireOp",EDGE,"E13.21.2"),sQuery(id+"F0.wireOp",EDGE,"E13.21.3"),sQuery(id+"F0.wireOp",EDGE,"E13.21.4"),sQuery(id+"F0.wireOp",EDGE,"E13.21.5"),sQuery(id+"F0.wireOp",EDGE,"E13.21.6"),sQuery(id+"F0.wireOp",EDGE,"E13.21.7"),sQuery(id+"F0.wireOp",EDGE,"E13.21.8"),sQuery(id+"F0.wireOp",EDGE,"E13.21.9"),sQuery(id+"F0.wireOp",EDGE,"E13.21.10"),sQuery(id+"F0.wireOp",EDGE,"E13.21.11"),sQuery(id+"F0.wireOp",EDGE,"E13.22.0"),sQuery(id+"F0.wireOp",EDGE,"E13.22.1"),sQuery(id+"F0.wireOp",EDGE,"E13.22.2"),sQuery(id+"F0.wireOp",EDGE,"E13.22.3"),sQuery(id+"F0.wireOp",EDGE,"E13.22.4"),sQuery(id+"F0.wireOp",EDGE,"E13.22.5"),sQuery(id+"F0.wireOp",EDGE,"E13.22.6"),sQuery(id+"F0.wireOp",EDGE,"E13.22.7"),sQuery(id+"F0.wireOp",EDGE,"E13.22.8"),sQuery(id+"F0.wireOp",EDGE,"E13.22.9"),sQuery(id+"F0.wireOp",EDGE,"E13.22.10"),sQuery(id+"F0.wireOp",EDGE,"E13.22.11"),sQuery(id+"F0.wireOp",EDGE,"E13.23.0"),sQuery(id+"F0.wireOp",EDGE,"E13.23.1"),sQuery(id+"F0.wireOp",EDGE,"E13.23.2"),sQuery(id+"F0.wireOp",EDGE,"E13.23.3"),sQuery(id+"F0.wireOp",EDGE,"E13.23.4"),sQuery(id+"F0.wireOp",EDGE,"E13.23.5"),sQuery(id+"F0.wireOp",EDGE,"E13.23.6"),sQuery(id+"F0.wireOp",EDGE,"E13.23.7"),sQuery(id+"F0.wireOp",EDGE,"E13.23.8"),sQuery(id+"F0.wireOp",EDGE,"E13.23.9"),sQuery(id+"F0.wireOp",EDGE,"E13.23.10"),sQuery(id+"F0.wireOp",EDGE,"E13.23.11"),sQuery(id+"F0.wireOp",EDGE,"E13.24.0"),sQuery(id+"F0.wireOp",EDGE,"E13.24.1"),sQuery(id+"F0.wireOp",EDGE,"E13.24.2"),sQuery(id+"F0.wireOp",EDGE,"E13.24.3"),sQuery(id+"F0.wireOp",EDGE,"E13.24.4"),sQuery(id+"F0.wireOp",EDGE,"E13.24.5"),sQuery(id+"F0.wireOp",EDGE,"E13.24.6"),sQuery(id+"F0.wireOp",EDGE,"E13.24.7"),sQuery(id+"F0.wireOp",EDGE,"E13.24.8"),sQuery(id+"F0.wireOp",EDGE,"E13.24.9"),sQuery(id+"F0.wireOp",EDGE,"E13.24.10"),sQuery(id+"F0.wireOp",EDGE,"E13.24.11"),sQuery(id+"F0.wireOp",EDGE,"E13.25.0"),sQuery(id+"F0.wireOp",EDGE,"E13.25.1"),sQuery(id+"F0.wireOp",EDGE,"E13.25.2"),sQuery(id+"F0.wireOp",EDGE,"E13.25.3"),sQuery(id+"F0.wireOp",EDGE,"E13.25.4"),sQuery(id+"F0.wireOp",EDGE,"E13.25.5"),sQuery(id+"F0.wireOp",EDGE,"E13.25.6"),sQuery(id+"F0.wireOp",EDGE,"E13.25.7"),sQuery(id+"F0.wireOp",EDGE,"E13.25.8"),sQuery(id+"F0.wireOp",EDGE,"E13.25.9"),sQuery(id+"F0.wireOp",EDGE,"E13.25.10"),sQuery(id+"F0.wireOp",EDGE,"E13.25.11"),sQuery(id+"F0.wireOp",EDGE,"E13.26.0"),sQuery(id+"F0.wireOp",EDGE,"E13.26.1"),sQuery(id+"F0.wireOp",EDGE,"E13.26.2"),sQuery(id+"F0.wireOp",EDGE,"E13.26.3"),sQuery(id+"F0.wireOp",EDGE,"E13.26.4"),sQuery(id+"F0.wireOp",EDGE,"E13.26.5"),sQuery(id+"F0.wireOp",EDGE,"E13.26.6"),sQuery(id+"F0.wireOp",EDGE,"E13.26.7"),sQuery(id+"F0.wireOp",EDGE,"E13.26.8"),sQuery(id+"F0.wireOp",EDGE,"E13.26.9"),sQuery(id+"F0.wireOp",EDGE,"E13.26.10"),sQuery(id+"F0.wireOp",EDGE,"E13.26.11"),sQuery(id+"F0.wireOp",EDGE,"E13.27.0"),sQuery(id+"F0.wireOp",EDGE,"E13.27.1"),sQuery(id+"F0.wireOp",EDGE,"E13.27.2"),sQuery(id+"F0.wireOp",EDGE,"E13.27.3"),sQuery(id+"F0.wireOp",EDGE,"E13.27.4"),sQuery(id+"F0.wireOp",EDGE,"E13.27.5"),sQuery(id+"F0.wireOp",EDGE,"E13.27.6"),sQuery(id+"F0.wireOp",EDGE,"E13.27.7"),sQuery(id+"F0.wireOp",EDGE,"E13.27.8"),sQuery(id+"F0.wireOp",EDGE,"E13.27.9"),sQuery(id+"F0.wireOp",EDGE,"E13.27.10"),sQuery(id+"F0.wireOp",EDGE,"E13.27.11"),sQuery(id+"F0.wireOp",EDGE,"E13.28.0"),sQuery(id+"F0.wireOp",EDGE,"E13.28.1"),sQuery(id+"F0.wireOp",EDGE,"E13.28.2"),sQuery(id+"F0.wireOp",EDGE,"E13.28.3"),sQuery(id+"F0.wireOp",EDGE,"E13.28.4"),sQuery(id+"F0.wireOp",EDGE,"E13.28.5"),sQuery(id+"F0.wireOp",EDGE,"E13.28.6"),sQuery(id+"F0.wireOp",EDGE,"E13.28.7"),sQuery(id+"F0.wireOp",EDGE,"E13.28.8"),sQuery(id+"F0.wireOp",EDGE,"E13.28.9"),sQuery(id+"F0.wireOp",EDGE,"E13.28.10"),sQuery(id+"F0.wireOp",EDGE,"E13.28.11"),sQuery(id+"F0.wireOp",EDGE,"E13.29.0"),sQuery(id+"F0.wireOp",EDGE,"E13.29.1"),sQuery(id+"F0.wireOp",EDGE,"E13.29.2"),sQuery(id+"F0.wireOp",EDGE,"E13.29.3"),sQuery(id+"F0.wireOp",EDGE,"E13.29.4"),sQuery(id+"F0.wireOp",EDGE,"E13.29.5"),sQuery(id+"F0.wireOp",EDGE,"E13.29.6"),sQuery(id+"F0.wireOp",EDGE,"E13.29.7"),sQuery(id+"F0.wireOp",EDGE,"E13.29.8"),sQuery(id+"F0.wireOp",EDGE,"E13.29.9"),sQuery(id+"F0.wireOp",EDGE,"E13.29.10"),sQuery(id+"F0.wireOp",EDGE,"E13.29.11"),sQuery(id+"F0.wireOp",EDGE,"E13.30.0"),sQuery(id+"F0.wireOp",EDGE,"E13.30.1"),sQuery(id+"F0.wireOp",EDGE,"E13.30.2"),sQuery(id+"F0.wireOp",EDGE,"E13.30.3"),sQuery(id+"F0.wireOp",EDGE,"E13.30.4"),sQuery(id+"F0.wireOp",EDGE,"E13.30.5"),sQuery(id+"F0.wireOp",EDGE,"E13.30.6"),sQuery(id+"F0.wireOp",EDGE,"E13.30.7"),sQuery(id+"F0.wireOp",EDGE,"E13.30.8"),sQuery(id+"F0.wireOp",EDGE,"E13.30.9"),sQuery(id+"F0.wireOp",EDGE,"E13.30.10"),sQuery(id+"F0.wireOp",EDGE,"E13.30.11"),sQuery(id+"F0.wireOp",EDGE,"E13.31.0"),sQuery(id+"F0.wireOp",EDGE,"E13.31.1"),sQuery(id+"F0.wireOp",EDGE,"E13.31.2"),sQuery(id+"F0.wireOp",EDGE,"E13.31.3"),sQuery(id+"F0.wireOp",EDGE,"E13.31.4"),sQuery(id+"F0.wireOp",EDGE,"E13.31.5"),sQuery(id+"F0.wireOp",EDGE,"E13.31.6"),sQuery(id+"F0.wireOp",EDGE,"E13.31.7"),sQuery(id+"F0.wireOp",EDGE,"E13.31.8"),sQuery(id+"F0.wireOp",EDGE,"E13.31.9"),sQuery(id+"F0.wireOp",EDGE,"E13.31.10"),sQuery(id+"F0.wireOp",EDGE,"E13.31.11"),sQuery(id+"F0.wireOp",EDGE,"E13.32.0"),sQuery(id+"F0.wireOp",EDGE,"E13.32.1"),sQuery(id+"F0.wireOp",EDGE,"E13.32.2"),sQuery(id+"F0.wireOp",EDGE,"E13.32.3"),sQuery(id+"F0.wireOp",EDGE,"E13.32.4"),sQuery(id+"F0.wireOp",EDGE,"E13.32.5"),sQuery(id+"F0.wireOp",EDGE,"E13.32.6"),sQuery(id+"F0.wireOp",EDGE,"E13.32.7"),sQuery(id+"F0.wireOp",EDGE,"E13.32.8"),sQuery(id+"F0.wireOp",EDGE,"E13.32.9"),sQuery(id+"F0.wireOp",EDGE,"E13.32.10"),sQuery(id+"F0.wireOp",EDGE,"E13.32.11"),sQuery(id+"F0.wireOp",EDGE,"E13.33.0"),sQuery(id+"F0.wireOp",EDGE,"E13.33.1"),sQuery(id+"F0.wireOp",EDGE,"E13.33.2"),sQuery(id+"F0.wireOp",EDGE,"E13.33.3"),sQuery(id+"F0.wireOp",EDGE,"E13.33.4"),sQuery(id+"F0.wireOp",EDGE,"E13.33.5"),sQuery(id+"F0.wireOp",EDGE,"E13.33.6"),sQuery(id+"F0.wireOp",EDGE,"E13.33.7"),sQuery(id+"F0.wireOp",EDGE,"E13.33.8"),sQuery(id+"F0.wireOp",EDGE,"E13.33.9"),sQuery(id+"F0.wireOp",EDGE,"E13.33.10"),sQuery(id+"F0.wireOp",EDGE,"E13.33.11"),sQuery(id+"F0.wireOp",EDGE,"E13.34.0"),sQuery(id+"F0.wireOp",EDGE,"E13.34.1"),sQuery(id+"F0.wireOp",EDGE,"E13.34.2"),sQuery(id+"F0.wireOp",EDGE,"E13.34.3"),sQuery(id+"F0.wireOp",EDGE,"E13.34.4"),sQuery(id+"F0.wireOp",EDGE,"E13.34.5"),sQuery(id+"F0.wireOp",EDGE,"E13.34.6"),sQuery(id+"F0.wireOp",EDGE,"E13.34.7"),sQuery(id+"F0.wireOp",EDGE,"E13.34.8"),sQuery(id+"F0.wireOp",EDGE,"E13.34.9"),sQuery(id+"F0.wireOp",EDGE,"E13.34.10"),sQuery(id+"F0.wireOp",EDGE,"E13.34.11"),sQuery(id+"F0.wireOp",EDGE,"E13.35.0"),sQuery(id+"F0.wireOp",EDGE,"E13.35.1"),sQuery(id+"F0.wireOp",EDGE,"E13.35.2"),sQuery(id+"F0.wireOp",EDGE,"E13.35.3"),sQuery(id+"F0.wireOp",EDGE,"E13.35.4"),sQuery(id+"F0.wireOp",EDGE,"E13.35.5"),sQuery(id+"F0.wireOp",EDGE,"E13.35.6"),sQuery(id+"F0.wireOp",EDGE,"E13.35.7"),sQuery(id+"F0.wireOp",EDGE,"E13.35.8"),sQuery(id+"F0.wireOp",EDGE,"E13.35.9"),sQuery(id+"F0.wireOp",EDGE,"E13.35.10"),sQuery(id+"F0.wireOp",EDGE,"E13.35.11"),sQuery(id+"F0.wireOp",EDGE,"E14.trimOffspring"),sQuery(id+"F0.wireOp",EDGE,"E15.trimOffspring"),sQuery(id+"F0.wireOp",EDGE,"E16.trimOffspring"),sQuery(id+"F0.wireOp",EDGE,"E17.trimOffspring"),sQuery(id+"F0.wireOp",EDGE,"E18.trimOffspring"),sQuery(id+"F0.wireOp",EDGE,"E19.trimOffspring"),sQuery(id+"F0.wireOp",EDGE,"E20.trimOffspring"),sQuery(id+"F0.wireOp",EDGE,"E21.trimOffspring"),sQuery(id+"F0.wireOp",EDGE,"E22.trimOffspring"),sQuery(id+"F0.wireOp",EDGE,"E23.trimOffspring"),sQuery(id+"F0.wireOp",EDGE,"E24.trimOffspring"),sQuery(id+"F0.wireOp",EDGE,"E25.trimOffspring"),sQuery(id+"F0.wireOp",EDGE,"E26.trimOffspring"),sQuery(id+"F0.wireOp",EDGE,"E27.trimOffspring"),sQuery(id+"F0.wireOp",EDGE,"E28.trimOffspring"),sQuery(id+"F0.wireOp",EDGE,"E29.trimOffspring"),sQuery(id+"F0.wireOp",EDGE,"E30.trimOffspring"),sQuery(id+"F0.wireOp",EDGE,"E31.trimOffspring"),sQuery(id+"F0.wireOp",EDGE,"E32.trimOffspring"),sQuery(id+"F0.wireOp",EDGE,"E33.trimOffspring"),sQuery(id+"F0.wireOp",EDGE,"E34.trimOffspring"),sQuery(id+"F0.wireOp",EDGE,"E35.trimOffspring"),sQuery(id+"F0.wireOp",EDGE,"E36.trimOffspring"),sQuery(id+"F0.wireOp",EDGE,"E37.trimOffspring"),sQuery(id+"F0.wireOp",EDGE,"E38.trimOffspring"),sQuery(id+"F0.wireOp",EDGE,"E39.trimOffspring"),sQuery(id+"F0.wireOp",EDGE,"E40.trimOffspring"),sQuery(id+"F0.wireOp",EDGE,"E41.trimOffspring"),sQuery(id+"F0.wireOp",EDGE,"E42.trimOffspring"),sQuery(id+"F0.wireOp",EDGE,"E43.trimOffspring"),sQuery(id+"F0.wireOp",EDGE,"E44.trimOffspring"),sQuery(id+"F0.wireOp",EDGE,"E45.trimOffspring"),sQuery(id+"F0.wireOp",EDGE,"E46.trimOffspring"),sQuery(id+"F0.wireOp",EDGE,"E47.trimOffspring"),sQuery(id+"F0.wireOp",EDGE,"E48.trimOffspring")])],"isStart":false});
            var sketch = newSketch(context, id + "F2", { "sketchPlane" : qUnion([Q0])});
            skCircle(sketch, "E49", {"center": v(0, 0) * mm, "radius": 3.17 * mm});
            skSolve(sketch);
        }
        {
            var Q0;
            Q0=makeQuery(id+"F2.imprint","IMPRINT",FACE,{"disambiguationData":[TD([[makeQuery(id+"F2.imprint","IMPRINT",EDGE,{"derivedFrom":sQuery(id+"F2.wireOp",EDGE,"E49")}),1.0]])]});
            extrude(context, id + "F3", {"entities" : qUnion([Q0]), "operationType" : NewBodyOperationType.REMOVE, "endBound" : BoundingType.THROUGH_ALL, "oppositeDirection" : true, "depth" : 25.4 * mm});
        }
    });
